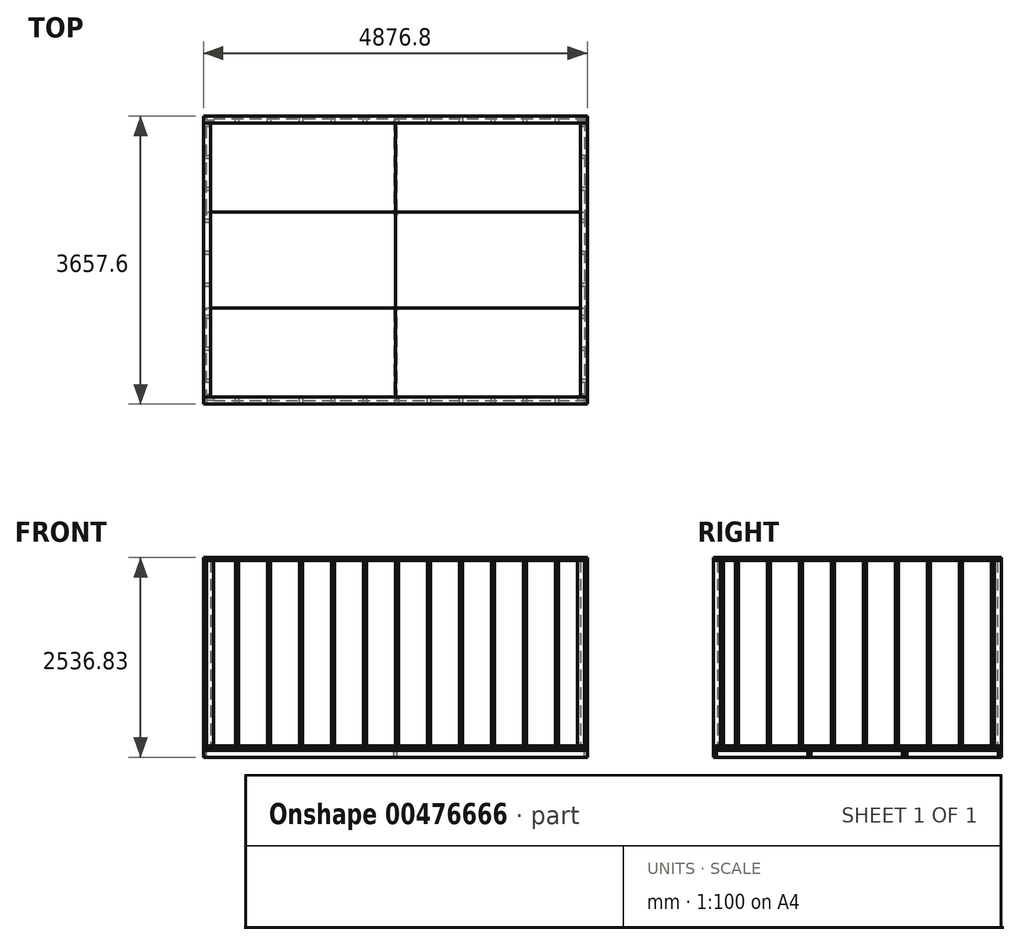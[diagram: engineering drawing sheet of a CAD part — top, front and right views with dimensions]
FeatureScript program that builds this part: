
annotation { "Feature Type Name" : "Feature", "Feature Type Description" : "" }
export const myFeature = defineFeature(function(context is Context, id is Id, definition is map)
    precondition{}
    {
        {
            var Q0;
            Q0=qCreatedBy(makeId("Top.planeOp"),FACE);
            var sketch = newSketch(context, id + "F0", { "sketchPlane" : qUnion([Q0])});
            skLineSegment(sketch, "E0.bottom", {"start": v(0, 0) * mm, "end": v(2438.4, 0) * mm});
            skLineSegment(sketch, "E0.top", {"start": v(0, 1219.2) * mm, "end": v(2438.4, 1219.2) * mm});
            skLineSegment(sketch, "E0.left", {"start": v(0, 0) * mm, "end": v(0, 1219.2) * mm});
            skLineSegment(sketch, "E0.right", {"start": v(2438.4, 0) * mm, "end": v(2438.4, 1219.2) * mm});
            skSolve(sketch);
        }
        {
            var Q0;
            Q0=makeQuery(id+"F0.imprint","IMPRINT",FACE,{"disambiguationData":[TD([[makeQuery(id+"F0.imprint","IMPRINT",EDGE,{"derivedFrom":sQuery(id+"F0.wireOp",EDGE,"E0.bottom")}),1.0]])]});
            extrude(context, id + "F1", {"entities" : qUnion([Q0]), "oppositeDirection" : true, "depth" : 19.05 * mm});
        }
        {
            var Q0;
            Q0=makeQuery(id+"F1.opExtrude","SWEPT_BODY",BODY,{"disambiguationData":[OSD([sQuery(id+"F0.wireOp",EDGE,"E0.bottom"),sQuery(id+"F0.wireOp",EDGE,"E0.top"),sQuery(id+"F0.wireOp",EDGE,"E0.left"),sQuery(id+"F0.wireOp",EDGE,"E0.right")])]});
            transform(context, id + "F2", {"entities" : qUnion([Q0]), "transformType" : TransformType.TRANSLATION_3D, "dx" : 2438.4 * mm, "dy" : 0 * mm, "dz" : 0 * mm, "makeCopy" : true});
        }
        {
            var Q0;
            Q0=makeQuery(id+"F1.opExtrude","SWEPT_BODY",BODY,{"disambiguationData":[OSD([sQuery(id+"F0.wireOp",EDGE,"E0.bottom"),sQuery(id+"F0.wireOp",EDGE,"E0.top"),sQuery(id+"F0.wireOp",EDGE,"E0.left"),sQuery(id+"F0.wireOp",EDGE,"E0.right")])]});
            transform(context, id + "F3", {"entities" : qUnion([Q0]), "transformType" : TransformType.TRANSLATION_3D, "dx" : 0 * mm, "dy" : 1219.2 * mm, "dz" : 0 * mm, "makeCopy" : true});
        }
        {
            var Q0;
            Q0=makeQuery(id+"F3.opPattern","COPY",BODY,{"derivedFrom":makeQuery(id+"F1.opExtrude","SWEPT_BODY",BODY,{"disambiguationData":[OSD([sQuery(id+"F0.wireOp",EDGE,"E0.bottom"),sQuery(id+"F0.wireOp",EDGE,"E0.top"),sQuery(id+"F0.wireOp",EDGE,"E0.left"),sQuery(id+"F0.wireOp",EDGE,"E0.right")])]}),"instanceName":"1"});
            transform(context, id + "F4", {"entities" : qUnion([Q0]), "transformType" : TransformType.TRANSLATION_3D, "dx" : 2438.4 * mm, "dy" : 0 * mm, "dz" : 0 * mm, "makeCopy" : true});
        }
        {
            var Q0;
            Q0=makeQuery(id+"F3.opPattern","COPY",BODY,{"derivedFrom":makeQuery(id+"F1.opExtrude","SWEPT_BODY",BODY,{"disambiguationData":[OSD([sQuery(id+"F0.wireOp",EDGE,"E0.bottom"),sQuery(id+"F0.wireOp",EDGE,"E0.top"),sQuery(id+"F0.wireOp",EDGE,"E0.left"),sQuery(id+"F0.wireOp",EDGE,"E0.right")])]}),"instanceName":"1"});
            transform(context, id + "F5", {"entities" : qUnion([Q0]), "transformType" : TransformType.TRANSLATION_3D, "dx" : 0 * mm, "dy" : 1219.2 * mm, "dz" : 0 * mm, "makeCopy" : true});
        }
        {
            var Q0;
            Q0=makeQuery(id+"F4.opPattern","COPY",BODY,{"derivedFrom":makeQuery(id+"F3.opPattern","COPY",BODY,{"derivedFrom":makeQuery(id+"F1.opExtrude","SWEPT_BODY",BODY,{"disambiguationData":[OSD([sQuery(id+"F0.wireOp",EDGE,"E0.bottom"),sQuery(id+"F0.wireOp",EDGE,"E0.top"),sQuery(id+"F0.wireOp",EDGE,"E0.left"),sQuery(id+"F0.wireOp",EDGE,"E0.right")])]}),"instanceName":"1"}),"instanceName":"1"});
            transform(context, id + "F6", {"entities" : qUnion([Q0]), "transformType" : TransformType.TRANSLATION_3D, "dx" : 0 * mm, "dy" : 1219.2 * mm, "dz" : 0 * mm, "makeCopy" : true});
        }
        {
            var Q0;
            Q0=qCreatedBy(makeId("Top.planeOp"),FACE);
            var sketch = newSketch(context, id + "F7", { "sketchPlane" : qUnion([Q0])});
            skLineSegment(sketch, "E1.bottom", {"start": v(0, 0) * mm, "end": v(4876.8, 0) * mm});
            skLineSegment(sketch, "E1.top", {"start": v(0, 88.9) * mm, "end": v(4876.8, 88.9) * mm});
            skLineSegment(sketch, "E1.left", {"start": v(0, 0) * mm, "end": v(0, 88.9) * mm});
            skLineSegment(sketch, "E1.right", {"start": v(4876.8, 0) * mm, "end": v(4876.8, 88.9) * mm});
            skSolve(sketch);
        }
        {
            var Q0;
            Q0 = qSketchRegion(id + "F7", true);
            extrude(context, id + "F8", {"entities" : qUnion([Q0]), "depth" : 38.1 * mm});
        }
        {
            var Q0;
            Q0=makeQuery(id+"F2.opPattern","COPY",FACE,{"derivedFrom":makeQuery(id+"F1.opExtrude","CAP_FACE",FACE,{"disambiguationData":[OSD([sQuery(id+"F0.wireOp",EDGE,"E0.bottom"),sQuery(id+"F0.wireOp",EDGE,"E0.top"),sQuery(id+"F0.wireOp",EDGE,"E0.left"),sQuery(id+"F0.wireOp",EDGE,"E0.right")])],"isStart":false}),"instanceName":"1"});
            var sketch = newSketch(context, id + "F9", { "sketchPlane" : qUnion([Q0])});
            skLineSegment(sketch, "E2.bottom", {"start": v(4876.8, 0) * mm, "end": v(0, 0) * mm});
            skLineSegment(sketch, "E2.top", {"start": v(4876.8, -38.1) * mm, "end": v(0, -38.1) * mm});
            skLineSegment(sketch, "E2.left", {"start": v(4876.8, 0) * mm, "end": v(4876.8, -38.1) * mm});
            skLineSegment(sketch, "E2.right", {"start": v(0, 0) * mm, "end": v(0, -38.1) * mm});
            skSolve(sketch);
        }
        {
            var Q0;
            Q0 = qSketchRegion(id + "F9", true);
            extrude(context, id + "F10", {"entities" : qUnion([Q0]), "depth" : 88.9 * mm});
        }
        {
            var Q0;
            Q0=makeQuery(id+"F10.opExtrude","SWEPT_BODY",BODY,{"disambiguationData":[OSD([sQuery(id+"F9.wireOp",EDGE,"E2.bottom"),sQuery(id+"F9.wireOp",EDGE,"E2.top"),sQuery(id+"F9.wireOp",EDGE,"E2.left"),sQuery(id+"F9.wireOp",EDGE,"E2.right")])]});
            transform(context, id + "F11", {"entities" : qUnion([Q0]), "transformType" : TransformType.TRANSLATION_3D, "dx" : 0 * mm, "dy" : 1200.15 * mm, "dz" : 0 * mm, "makeCopy" : true});
        }
        {
            var Q0;
            Q0=makeQuery(id+"F11.opPattern","COPY",BODY,{"derivedFrom":makeQuery(id+"F10.opExtrude","SWEPT_BODY",BODY,{"disambiguationData":[OSD([sQuery(id+"F9.wireOp",EDGE,"E2.bottom"),sQuery(id+"F9.wireOp",EDGE,"E2.top"),sQuery(id+"F9.wireOp",EDGE,"E2.left"),sQuery(id+"F9.wireOp",EDGE,"E2.right")])]}),"instanceName":"1"});
            transform(context, id + "F12", {"entities" : qUnion([Q0]), "transformType" : TransformType.TRANSLATION_3D, "dx" : 0 * mm, "dy" : 1219.2 * mm, "dz" : 0 * mm, "makeCopy" : true});
        }
        {
            var Q0;
            Q0=makeQuery(id+"F12.opPattern","COPY",BODY,{"derivedFrom":makeQuery(id+"F11.opPattern","COPY",BODY,{"derivedFrom":makeQuery(id+"F10.opExtrude","SWEPT_BODY",BODY,{"disambiguationData":[OSD([sQuery(id+"F9.wireOp",EDGE,"E2.bottom"),sQuery(id+"F9.wireOp",EDGE,"E2.top"),sQuery(id+"F9.wireOp",EDGE,"E2.left"),sQuery(id+"F9.wireOp",EDGE,"E2.right")])]}),"instanceName":"1"}),"instanceName":"1"});
            transform(context, id + "F13", {"entities" : qUnion([Q0]), "transformType" : TransformType.TRANSLATION_3D, "dx" : 0 * mm, "dy" : 1200.15 * mm, "dz" : 0 * mm, "makeCopy" : true});
        }
        {
            var Q0;
            Q0=makeQuery(id+"F6.opPattern","COPY",FACE,{"derivedFrom":makeQuery(id+"F4.opPattern","COPY",FACE,{"derivedFrom":makeQuery(id+"F3.opPattern","COPY",FACE,{"derivedFrom":makeQuery(id+"F1.opExtrude","CAP_FACE",FACE,{"disambiguationData":[OSD([sQuery(id+"F0.wireOp",EDGE,"E0.bottom"),sQuery(id+"F0.wireOp",EDGE,"E0.top"),sQuery(id+"F0.wireOp",EDGE,"E0.left"),sQuery(id+"F0.wireOp",EDGE,"E0.right")])],"isStart":false}),"instanceName":"1"}),"instanceName":"1"}),"instanceName":"1"});
            var sketch = newSketch(context, id + "F14", { "sketchPlane" : qUnion([Q0])});
            skLineSegment(sketch, "E3.bottom", {"start": v(4876.8, -3617.88) * mm, "end": v(4838.7, -3617.88) * mm});
            skLineSegment(sketch, "E3.top", {"start": v(4876.8, -2455.83) * mm, "end": v(4838.7, -2455.83) * mm});
            skLineSegment(sketch, "E3.left", {"start": v(4876.8, -3617.88) * mm, "end": v(4876.8, -2455.83) * mm});
            skLineSegment(sketch, "E3.right", {"start": v(4838.7, -3617.88) * mm, "end": v(4838.7, -2455.83) * mm});
            skSolve(sketch);
        }
        {
            var Q0;
            Q0 = qSketchRegion(id + "F14", true);
            extrude(context, id + "F15", {"entities" : qUnion([Q0]), "depth" : 88.9 * mm});
        }
        {
            var Q0;
            Q0=makeQuery(id+"F15.opExtrude","SWEPT_BODY",BODY,{"disambiguationData":[OSD([sQuery(id+"F14.wireOp",EDGE,"E3.bottom"),sQuery(id+"F14.wireOp",EDGE,"E3.top"),sQuery(id+"F14.wireOp",EDGE,"E3.left"),sQuery(id+"F14.wireOp",EDGE,"E3.right")])]});
            var Q1;
            Q1=makeQuery(id+"F15.opExtrude","CAP_VERTEX",VERTEX,{"disambiguationData":[OSD([sQuery(id+"F0.wireOp",EDGE,"E0.right"),sQuery(id+"F14.wireOp",EDGE,"E3.bottom"),sQuery(id+"F14.wireOp",EDGE,"E3.left")])],"isStart":true});
            var Q2;
            Q2=makeQuery(id+"F13.opPattern","COPY",VERTEX,{"derivedFrom":makeQuery(id+"F12.opPattern","COPY",VERTEX,{"derivedFrom":makeQuery(id+"F11.opPattern","COPY",VERTEX,{"derivedFrom":makeQuery(id+"F10.opExtrude","CAP_VERTEX",VERTEX,{"disambiguationData":[OSD([sQuery(id+"F9.wireOp",EDGE,"E2.bottom"),sQuery(id+"F9.wireOp",EDGE,"E2.left")])],"isStart":true}),"instanceName":"1"}),"instanceName":"1"}),"instanceName":"1"});
            transform(context, id + "F16", {"entities" : qUnion([Q0]), "transformType" : TransformType.TRANSLATION_ENTITY, "oppositeDirectionEntity" : false, "transformLine" : qUnion([Q1, Q2]), "makeCopy" : false});
        }
        {
            var Q0;
            Q0=makeQuery(id+"F15.opExtrude","SWEPT_BODY",BODY,{"disambiguationData":[OSD([sQuery(id+"F14.wireOp",EDGE,"E3.bottom"),sQuery(id+"F14.wireOp",EDGE,"E3.top"),sQuery(id+"F14.wireOp",EDGE,"E3.left"),sQuery(id+"F14.wireOp",EDGE,"E3.right")])]});
            transform(context, id + "F17", {"entities" : qUnion([Q0]), "transformType" : TransformType.TRANSLATION_3D, "dx" : -2438.4 * mm, "dy" : 0 * mm, "dz" : 0 * mm, "makeCopy" : true});
        }
        {
            var Q0;
            Q0=makeQuery(id+"F17.opPattern","COPY",BODY,{"derivedFrom":makeQuery(id+"F15.opExtrude","SWEPT_BODY",BODY,{"disambiguationData":[OSD([sQuery(id+"F14.wireOp",EDGE,"E3.bottom"),sQuery(id+"F14.wireOp",EDGE,"E3.top"),sQuery(id+"F14.wireOp",EDGE,"E3.left"),sQuery(id+"F14.wireOp",EDGE,"E3.right")])]}),"instanceName":"1"});
            transform(context, id + "F18", {"entities" : qUnion([Q0]), "transformType" : TransformType.TRANSLATION_3D, "dx" : 19.05 * mm, "dy" : 0 * mm, "dz" : 0 * mm, "makeCopy" : false});
        }
        {
            var Q0;
            Q0=makeQuery(id+"F17.opPattern","COPY",BODY,{"derivedFrom":makeQuery(id+"F15.opExtrude","SWEPT_BODY",BODY,{"disambiguationData":[OSD([sQuery(id+"F14.wireOp",EDGE,"E3.bottom"),sQuery(id+"F14.wireOp",EDGE,"E3.top"),sQuery(id+"F14.wireOp",EDGE,"E3.left"),sQuery(id+"F14.wireOp",EDGE,"E3.right")])]}),"instanceName":"1"});
            transform(context, id + "F19", {"entities" : qUnion([Q0]), "transformType" : TransformType.TRANSLATION_3D, "dx" : -2419.35 * mm, "dy" : 0 * mm, "dz" : 0 * mm, "makeCopy" : true});
        }
        {
            var Q0;
            Q0=makeQuery(id+"F15.opExtrude","SWEPT_BODY",BODY,{"disambiguationData":[OSD([sQuery(id+"F14.wireOp",EDGE,"E3.bottom"),sQuery(id+"F14.wireOp",EDGE,"E3.top"),sQuery(id+"F14.wireOp",EDGE,"E3.left"),sQuery(id+"F14.wireOp",EDGE,"E3.right")])]});
            transform(context, id + "F20", {"entities" : qUnion([Q0]), "transformType" : TransformType.TRANSLATION_3D, "dx" : 0 * mm, "dy" : -1257.3 * mm, "dz" : 0 * mm, "makeCopy" : true});
        }
        {
            var Q0;
            Q0=makeQuery(id+"F20.opPattern","COPY",BODY,{"derivedFrom":makeQuery(id+"F15.opExtrude","SWEPT_BODY",BODY,{"disambiguationData":[OSD([sQuery(id+"F14.wireOp",EDGE,"E3.bottom"),sQuery(id+"F14.wireOp",EDGE,"E3.top"),sQuery(id+"F14.wireOp",EDGE,"E3.left"),sQuery(id+"F14.wireOp",EDGE,"E3.right")])]}),"instanceName":"1"});
            transform(context, id + "F21", {"entities" : qUnion([Q0]), "transformType" : TransformType.TRANSLATION_3D, "dx" : 0 * mm, "dy" : 38.1 * mm, "dz" : 0 * mm, "makeCopy" : false});
        }
        {
            var Q0;
            Q0=makeQuery(id+"F20.opPattern","COPY",BODY,{"derivedFrom":makeQuery(id+"F15.opExtrude","SWEPT_BODY",BODY,{"disambiguationData":[OSD([sQuery(id+"F14.wireOp",EDGE,"E3.bottom"),sQuery(id+"F14.wireOp",EDGE,"E3.top"),sQuery(id+"F14.wireOp",EDGE,"E3.left"),sQuery(id+"F14.wireOp",EDGE,"E3.right")])]}),"instanceName":"1"});
            deleteBodies(context, id + "F22", {"entities" : qUnion([Q0])});
        }
        {
            var Q0;
            Q0=makeQuery(id+"F19.opPattern","COPY",BODY,{"derivedFrom":makeQuery(id+"F17.opPattern","COPY",BODY,{"derivedFrom":makeQuery(id+"F15.opExtrude","SWEPT_BODY",BODY,{"disambiguationData":[OSD([sQuery(id+"F14.wireOp",EDGE,"E3.bottom"),sQuery(id+"F14.wireOp",EDGE,"E3.top"),sQuery(id+"F14.wireOp",EDGE,"E3.left"),sQuery(id+"F14.wireOp",EDGE,"E3.right")])]}),"instanceName":"1"}),"instanceName":"1"});
            transform(context, id + "F23", {"entities" : qUnion([Q0]), "transformType" : TransformType.TRANSLATION_3D, "dx" : 0 * mm, "dy" : -2400.3 * mm, "dz" : 0 * mm, "makeCopy" : true});
        }
        {
            var Q0;
            Q0=makeQuery(id+"F23.opPattern","COPY",BODY,{"derivedFrom":makeQuery(id+"F19.opPattern","COPY",BODY,{"derivedFrom":makeQuery(id+"F17.opPattern","COPY",BODY,{"derivedFrom":makeQuery(id+"F15.opExtrude","SWEPT_BODY",BODY,{"disambiguationData":[OSD([sQuery(id+"F14.wireOp",EDGE,"E3.bottom"),sQuery(id+"F14.wireOp",EDGE,"E3.top"),sQuery(id+"F14.wireOp",EDGE,"E3.left"),sQuery(id+"F14.wireOp",EDGE,"E3.right")])]}),"instanceName":"1"}),"instanceName":"1"}),"instanceName":"1"});
            transform(context, id + "F24", {"entities" : qUnion([Q0]), "transformType" : TransformType.TRANSLATION_3D, "dx" : 0 * mm, "dy" : -19.05 * mm, "dz" : 0 * mm, "makeCopy" : false});
        }
        {
            var Q0;
            Q0=makeQuery(id+"F17.opPattern","COPY",BODY,{"derivedFrom":makeQuery(id+"F15.opExtrude","SWEPT_BODY",BODY,{"disambiguationData":[OSD([sQuery(id+"F14.wireOp",EDGE,"E3.bottom"),sQuery(id+"F14.wireOp",EDGE,"E3.top"),sQuery(id+"F14.wireOp",EDGE,"E3.left"),sQuery(id+"F14.wireOp",EDGE,"E3.right")])]}),"instanceName":"1"});
            transform(context, id + "F25", {"entities" : qUnion([Q0]), "transformType" : TransformType.TRANSLATION_3D, "dx" : 0 * mm, "dy" : -2419.35 * mm, "dz" : 0 * mm, "makeCopy" : true});
        }
        {
            var Q0;
            Q0=makeQuery(id+"F15.opExtrude","SWEPT_BODY",BODY,{"disambiguationData":[OSD([sQuery(id+"F14.wireOp",EDGE,"E3.bottom"),sQuery(id+"F14.wireOp",EDGE,"E3.top"),sQuery(id+"F14.wireOp",EDGE,"E3.left"),sQuery(id+"F14.wireOp",EDGE,"E3.right")])]});
            transform(context, id + "F26", {"entities" : qUnion([Q0]), "transformType" : TransformType.TRANSLATION_3D, "dx" : 0 * mm, "dy" : -2419.35 * mm, "dz" : 0 * mm, "makeCopy" : true});
        }
        {
            var Q0;
            Q0=makeQuery(id+"F4.opPattern","COPY",FACE,{"derivedFrom":makeQuery(id+"F3.opPattern","COPY",FACE,{"derivedFrom":makeQuery(id+"F1.opExtrude","CAP_FACE",FACE,{"disambiguationData":[OSD([sQuery(id+"F0.wireOp",EDGE,"E0.bottom"),sQuery(id+"F0.wireOp",EDGE,"E0.top"),sQuery(id+"F0.wireOp",EDGE,"E0.left"),sQuery(id+"F0.wireOp",EDGE,"E0.right")])],"isStart":false}),"instanceName":"1"}),"instanceName":"1"});
            var sketch = newSketch(context, id + "F27", { "sketchPlane" : qUnion([Q0])});
            skSolve(sketch);
        }
        {
            var Q0;
            Q0=makeQuery(id+"F15.opExtrude","SWEPT_BODY",BODY,{"disambiguationData":[OSD([sQuery(id+"F14.wireOp",EDGE,"E3.bottom"),sQuery(id+"F14.wireOp",EDGE,"E3.top"),sQuery(id+"F14.wireOp",EDGE,"E3.left"),sQuery(id+"F14.wireOp",EDGE,"E3.right")])]});
            transform(context, id + "F28", {"entities" : qUnion([Q0]), "transformType" : TransformType.TRANSLATION_3D, "dx" : 0 * mm, "dy" : -1219.2 * mm, "dz" : 0 * mm, "makeCopy" : true});
        }
        {
            var Q0;
            Q0=makeQuery(id+"F28.opPattern","COPY",FACE,{"derivedFrom":makeQuery(id+"F15.opExtrude","SWEPT_FACE",FACE,{"disambiguationData":[OSD([sQuery(id+"F14.wireOp",EDGE,"E3.bottom")])]}),"instanceName":"1"});
            extrude(context, id + "F29", {"entities" : qUnion([Q0]), "depth" : 19.05 * mm});
        }
        {
            var Q0;
            Q0=makeQuery(id+"F29.opExtrude","SWEPT_BODY",BODY,{"disambiguationData":[OSD([sQuery(id+"F14.wireOp",EDGE,"E3.bottom")])]});
            transform(context, id + "F30", {"entities" : qUnion([Q0]), "transformType" : TransformType.TRANSLATION_3D, "dx" : -2419.35 * mm, "dy" : 0 * mm, "dz" : 0 * mm, "makeCopy" : true});
        }
        {
            var Q0;
            Q0=makeQuery(id+"F30.opPattern","COPY",BODY,{"derivedFrom":makeQuery(id+"F29.opExtrude","SWEPT_BODY",BODY,{"disambiguationData":[OSD([sQuery(id+"F14.wireOp",EDGE,"E3.bottom")])]}),"instanceName":"1"});
            transform(context, id + "F31", {"entities" : qUnion([Q0]), "transformType" : TransformType.TRANSLATION_3D, "dx" : -2419.35 * mm, "dy" : 0 * mm, "dz" : 0 * mm, "makeCopy" : true});
        }
        {
            var Q0;
            Q0=makeQuery(id+"F8.opExtrude","SWEPT_BODY",BODY,{"disambiguationData":[OSD([sQuery(id+"F7.wireOp",EDGE,"E1.bottom"),sQuery(id+"F7.wireOp",EDGE,"E1.top"),sQuery(id+"F7.wireOp",EDGE,"E1.left"),sQuery(id+"F7.wireOp",EDGE,"E1.right")])]});
            transform(context, id + "F32", {"entities" : qUnion([Q0]), "transformType" : TransformType.TRANSLATION_3D, "dx" : 0 * mm, "dy" : 3568.7 * mm, "dz" : 0 * mm, "makeCopy" : true});
        }
        {
            var Q0;
            Q0=makeQuery(id+"F32.opPattern","COPY",FACE,{"derivedFrom":makeQuery(id+"F8.opExtrude","CAP_FACE",FACE,{"disambiguationData":[OSD([sQuery(id+"F7.wireOp",EDGE,"E1.bottom"),sQuery(id+"F7.wireOp",EDGE,"E1.top"),sQuery(id+"F7.wireOp",EDGE,"E1.left"),sQuery(id+"F7.wireOp",EDGE,"E1.right")])],"isStart":false}),"instanceName":"1"});
            var sketch = newSketch(context, id + "F33", { "sketchPlane" : qUnion([Q0])});
            skLineSegment(sketch, "E4.bottom", {"start": v(0, 3568.7) * mm, "end": v(88.9, 3568.7) * mm});
            skLineSegment(sketch, "E4.top", {"start": v(0, 88.9) * mm, "end": v(88.9, 88.9) * mm});
            skLineSegment(sketch, "E4.left", {"start": v(0, 3568.7) * mm, "end": v(0, 88.9) * mm});
            skLineSegment(sketch, "E4.right", {"start": v(88.9, 3568.7) * mm, "end": v(88.9, 88.9) * mm});
            skSolve(sketch);
        }
        {
            var Q0;
            Q0=makeQuery(id+"F33.imprint","IMPRINT",FACE,{"disambiguationData":[TD([[makeQuery(id+"F33.imprint","IMPRINT",EDGE,{"derivedFrom":sQuery(id+"F33.wireOp",EDGE,"E4.bottom")}),-1.0]])]});
            extrude(context, id + "F34", {"entities" : qUnion([Q0]), "depth" : -38.1 * mm});
        }
        {
            var Q0;
            Q0=makeQuery(id+"F34.opExtrude","SWEPT_BODY",BODY,{"disambiguationData":[OSD([sQuery(id+"F33.wireOp",EDGE,"E4.bottom"),sQuery(id+"F33.wireOp",EDGE,"E4.top"),sQuery(id+"F33.wireOp",EDGE,"E4.left"),sQuery(id+"F33.wireOp",EDGE,"E4.right")])]});
            transform(context, id + "F35", {"entities" : qUnion([Q0]), "transformType" : TransformType.TRANSLATION_3D, "dx" : 4787.9 * mm, "dy" : 0 * mm, "dz" : 0 * mm, "makeCopy" : true});
        }
        {
            var Q0;
            Q0=makeQuery(id+"F32.opPattern","COPY",FACE,{"derivedFrom":makeQuery(id+"F8.opExtrude","CAP_FACE",FACE,{"disambiguationData":[OSD([sQuery(id+"F7.wireOp",EDGE,"E1.bottom"),sQuery(id+"F7.wireOp",EDGE,"E1.top"),sQuery(id+"F7.wireOp",EDGE,"E1.left"),sQuery(id+"F7.wireOp",EDGE,"E1.right")])],"isStart":false}),"instanceName":"1"});
            var sketch = newSketch(context, id + "F36", { "sketchPlane" : qUnion([Q0])});
            skLineSegment(sketch, "E5.bottom", {"start": v(0, 3657.6) * mm, "end": v(38.1, 3657.6) * mm});
            skLineSegment(sketch, "E5.top", {"start": v(0, 3568.7) * mm, "end": v(38.1, 3568.7) * mm});
            skLineSegment(sketch, "E5.left", {"start": v(0, 3657.6) * mm, "end": v(0, 3568.7) * mm});
            skLineSegment(sketch, "E5.right", {"start": v(38.1, 3657.6) * mm, "end": v(38.1, 3568.7) * mm});
            skSolve(sketch);
        }
        {
            var Q0;
            Q0=makeQuery(id+"F36.imprint","IMPRINT",FACE,{"disambiguationData":[TD([[makeQuery(id+"F36.imprint","IMPRINT",EDGE,{"derivedFrom":sQuery(id+"F36.wireOp",EDGE,"E5.bottom")}),-1.0]])]});
            extrude(context, id + "F37", {"entities" : qUnion([Q0]), "depth" : 2352.67 * mm});
        }
        {
            var Q0;
            Q0=makeQuery(id+"F37.opExtrude","SWEPT_BODY",BODY,{"disambiguationData":[OSD([sQuery(id+"F36.wireOp",EDGE,"E5.bottom"),sQuery(id+"F36.wireOp",EDGE,"E5.top"),sQuery(id+"F36.wireOp",EDGE,"E5.left"),sQuery(id+"F36.wireOp",EDGE,"E5.right")])]});
            transform(context, id + "F38", {"entities" : qUnion([Q0]), "transformType" : TransformType.TRANSLATION_3D, "dx" : 406.4 * mm, "dy" : 0 * mm, "dz" : 0 * mm, "makeCopy" : true});
        }
        {
            var Q0;
            Q0=makeQuery(id+"F38.opPattern","COPY",BODY,{"derivedFrom":makeQuery(id+"F37.opExtrude","SWEPT_BODY",BODY,{"disambiguationData":[OSD([sQuery(id+"F36.wireOp",EDGE,"E5.bottom"),sQuery(id+"F36.wireOp",EDGE,"E5.top"),sQuery(id+"F36.wireOp",EDGE,"E5.left"),sQuery(id+"F36.wireOp",EDGE,"E5.right")])]}),"instanceName":"1"});
            transform(context, id + "F39", {"entities" : qUnion([Q0]), "transformType" : TransformType.TRANSLATION_3D, "dx" : 406.4 * mm, "dy" : 0 * mm, "dz" : 0 * mm, "makeCopy" : true});
        }
        {
            var Q0;
            Q0=makeQuery(id+"F39.opPattern","COPY",BODY,{"derivedFrom":makeQuery(id+"F38.opPattern","COPY",BODY,{"derivedFrom":makeQuery(id+"F37.opExtrude","SWEPT_BODY",BODY,{"disambiguationData":[OSD([sQuery(id+"F36.wireOp",EDGE,"E5.bottom"),sQuery(id+"F36.wireOp",EDGE,"E5.top"),sQuery(id+"F36.wireOp",EDGE,"E5.left"),sQuery(id+"F36.wireOp",EDGE,"E5.right")])]}),"instanceName":"1"}),"instanceName":"1"});
            transform(context, id + "F40", {"entities" : qUnion([Q0]), "transformType" : TransformType.TRANSLATION_3D, "dx" : 406.4 * mm, "dy" : 0 * mm, "dz" : 0 * mm, "makeCopy" : true});
        }
        {
            var Q0;
            Q0=makeQuery(id+"F40.opPattern","COPY",BODY,{"derivedFrom":makeQuery(id+"F39.opPattern","COPY",BODY,{"derivedFrom":makeQuery(id+"F38.opPattern","COPY",BODY,{"derivedFrom":makeQuery(id+"F37.opExtrude","SWEPT_BODY",BODY,{"disambiguationData":[OSD([sQuery(id+"F36.wireOp",EDGE,"E5.bottom"),sQuery(id+"F36.wireOp",EDGE,"E5.top"),sQuery(id+"F36.wireOp",EDGE,"E5.left"),sQuery(id+"F36.wireOp",EDGE,"E5.right")])]}),"instanceName":"1"}),"instanceName":"1"}),"instanceName":"1"});
            transform(context, id + "F41", {"entities" : qUnion([Q0]), "transformType" : TransformType.TRANSLATION_3D, "dx" : 406.4 * mm, "dy" : 0 * mm, "dz" : 0 * mm, "makeCopy" : true});
        }
        {
            var Q0;
            Q0=makeQuery(id+"F41.opPattern","COPY",BODY,{"derivedFrom":makeQuery(id+"F40.opPattern","COPY",BODY,{"derivedFrom":makeQuery(id+"F39.opPattern","COPY",BODY,{"derivedFrom":makeQuery(id+"F38.opPattern","COPY",BODY,{"derivedFrom":makeQuery(id+"F37.opExtrude","SWEPT_BODY",BODY,{"disambiguationData":[OSD([sQuery(id+"F36.wireOp",EDGE,"E5.bottom"),sQuery(id+"F36.wireOp",EDGE,"E5.top"),sQuery(id+"F36.wireOp",EDGE,"E5.left"),sQuery(id+"F36.wireOp",EDGE,"E5.right")])]}),"instanceName":"1"}),"instanceName":"1"}),"instanceName":"1"}),"instanceName":"1"});
            transform(context, id + "F42", {"entities" : qUnion([Q0]), "transformType" : TransformType.TRANSLATION_3D, "dx" : 406.4 * mm, "dy" : 0 * mm, "dz" : 0 * mm, "makeCopy" : true});
        }
        {
            var Q0;
            Q0=makeQuery(id+"F42.opPattern","COPY",BODY,{"derivedFrom":makeQuery(id+"F41.opPattern","COPY",BODY,{"derivedFrom":makeQuery(id+"F40.opPattern","COPY",BODY,{"derivedFrom":makeQuery(id+"F39.opPattern","COPY",BODY,{"derivedFrom":makeQuery(id+"F38.opPattern","COPY",BODY,{"derivedFrom":makeQuery(id+"F37.opExtrude","SWEPT_BODY",BODY,{"disambiguationData":[OSD([sQuery(id+"F36.wireOp",EDGE,"E5.bottom"),sQuery(id+"F36.wireOp",EDGE,"E5.top"),sQuery(id+"F36.wireOp",EDGE,"E5.left"),sQuery(id+"F36.wireOp",EDGE,"E5.right")])]}),"instanceName":"1"}),"instanceName":"1"}),"instanceName":"1"}),"instanceName":"1"}),"instanceName":"1"});
            transform(context, id + "F43", {"entities" : qUnion([Q0]), "transformType" : TransformType.TRANSLATION_3D, "dx" : 406.4 * mm, "dy" : 0 * mm, "dz" : 0 * mm, "makeCopy" : true});
        }
        {
            var Q0;
            Q0=makeQuery(id+"F43.opPattern","COPY",BODY,{"derivedFrom":makeQuery(id+"F42.opPattern","COPY",BODY,{"derivedFrom":makeQuery(id+"F41.opPattern","COPY",BODY,{"derivedFrom":makeQuery(id+"F40.opPattern","COPY",BODY,{"derivedFrom":makeQuery(id+"F39.opPattern","COPY",BODY,{"derivedFrom":makeQuery(id+"F38.opPattern","COPY",BODY,{"derivedFrom":makeQuery(id+"F37.opExtrude","SWEPT_BODY",BODY,{"disambiguationData":[OSD([sQuery(id+"F36.wireOp",EDGE,"E5.bottom"),sQuery(id+"F36.wireOp",EDGE,"E5.top"),sQuery(id+"F36.wireOp",EDGE,"E5.left"),sQuery(id+"F36.wireOp",EDGE,"E5.right")])]}),"instanceName":"1"}),"instanceName":"1"}),"instanceName":"1"}),"instanceName":"1"}),"instanceName":"1"}),"instanceName":"1"});
            transform(context, id + "F44", {"entities" : qUnion([Q0]), "transformType" : TransformType.TRANSLATION_3D, "dx" : 406.4 * mm, "dy" : 0 * mm, "dz" : 0 * mm, "makeCopy" : true});
        }
        {
            var Q0;
            Q0=makeQuery(id+"F44.opPattern","COPY",BODY,{"derivedFrom":makeQuery(id+"F43.opPattern","COPY",BODY,{"derivedFrom":makeQuery(id+"F42.opPattern","COPY",BODY,{"derivedFrom":makeQuery(id+"F41.opPattern","COPY",BODY,{"derivedFrom":makeQuery(id+"F40.opPattern","COPY",BODY,{"derivedFrom":makeQuery(id+"F39.opPattern","COPY",BODY,{"derivedFrom":makeQuery(id+"F38.opPattern","COPY",BODY,{"derivedFrom":makeQuery(id+"F37.opExtrude","SWEPT_BODY",BODY,{"disambiguationData":[OSD([sQuery(id+"F36.wireOp",EDGE,"E5.bottom"),sQuery(id+"F36.wireOp",EDGE,"E5.top"),sQuery(id+"F36.wireOp",EDGE,"E5.left"),sQuery(id+"F36.wireOp",EDGE,"E5.right")])]}),"instanceName":"1"}),"instanceName":"1"}),"instanceName":"1"}),"instanceName":"1"}),"instanceName":"1"}),"instanceName":"1"}),"instanceName":"1"});
            transform(context, id + "F45", {"entities" : qUnion([Q0]), "transformType" : TransformType.TRANSLATION_3D, "dx" : 406.4 * mm, "dy" : 0 * mm, "dz" : 0 * mm, "makeCopy" : true});
        }
        {
            var Q0;
            Q0=makeQuery(id+"F45.opPattern","COPY",BODY,{"derivedFrom":makeQuery(id+"F44.opPattern","COPY",BODY,{"derivedFrom":makeQuery(id+"F43.opPattern","COPY",BODY,{"derivedFrom":makeQuery(id+"F42.opPattern","COPY",BODY,{"derivedFrom":makeQuery(id+"F41.opPattern","COPY",BODY,{"derivedFrom":makeQuery(id+"F40.opPattern","COPY",BODY,{"derivedFrom":makeQuery(id+"F39.opPattern","COPY",BODY,{"derivedFrom":makeQuery(id+"F38.opPattern","COPY",BODY,{"derivedFrom":makeQuery(id+"F37.opExtrude","SWEPT_BODY",BODY,{"disambiguationData":[OSD([sQuery(id+"F36.wireOp",EDGE,"E5.bottom"),sQuery(id+"F36.wireOp",EDGE,"E5.top"),sQuery(id+"F36.wireOp",EDGE,"E5.left"),sQuery(id+"F36.wireOp",EDGE,"E5.right")])]}),"instanceName":"1"}),"instanceName":"1"}),"instanceName":"1"}),"instanceName":"1"}),"instanceName":"1"}),"instanceName":"1"}),"instanceName":"1"}),"instanceName":"1"});
            transform(context, id + "F46", {"entities" : qUnion([Q0]), "transformType" : TransformType.TRANSLATION_3D, "dx" : 406.4 * mm, "dy" : 0 * mm, "dz" : 0 * mm, "makeCopy" : true});
        }
        {
            var Q0;
            Q0=makeQuery(id+"F46.opPattern","COPY",BODY,{"derivedFrom":makeQuery(id+"F45.opPattern","COPY",BODY,{"derivedFrom":makeQuery(id+"F44.opPattern","COPY",BODY,{"derivedFrom":makeQuery(id+"F43.opPattern","COPY",BODY,{"derivedFrom":makeQuery(id+"F42.opPattern","COPY",BODY,{"derivedFrom":makeQuery(id+"F41.opPattern","COPY",BODY,{"derivedFrom":makeQuery(id+"F40.opPattern","COPY",BODY,{"derivedFrom":makeQuery(id+"F39.opPattern","COPY",BODY,{"derivedFrom":makeQuery(id+"F38.opPattern","COPY",BODY,{"derivedFrom":makeQuery(id+"F37.opExtrude","SWEPT_BODY",BODY,{"disambiguationData":[OSD([sQuery(id+"F36.wireOp",EDGE,"E5.bottom"),sQuery(id+"F36.wireOp",EDGE,"E5.top"),sQuery(id+"F36.wireOp",EDGE,"E5.left"),sQuery(id+"F36.wireOp",EDGE,"E5.right")])]}),"instanceName":"1"}),"instanceName":"1"}),"instanceName":"1"}),"instanceName":"1"}),"instanceName":"1"}),"instanceName":"1"}),"instanceName":"1"}),"instanceName":"1"}),"instanceName":"1"});
            transform(context, id + "F47", {"entities" : qUnion([Q0]), "transformType" : TransformType.TRANSLATION_3D, "dx" : 406.4 * mm, "dy" : 0 * mm, "dz" : 0 * mm, "makeCopy" : true});
        }
        {
            var Q0;
            Q0=makeQuery(id+"F47.opPattern","COPY",BODY,{"derivedFrom":makeQuery(id+"F46.opPattern","COPY",BODY,{"derivedFrom":makeQuery(id+"F45.opPattern","COPY",BODY,{"derivedFrom":makeQuery(id+"F44.opPattern","COPY",BODY,{"derivedFrom":makeQuery(id+"F43.opPattern","COPY",BODY,{"derivedFrom":makeQuery(id+"F42.opPattern","COPY",BODY,{"derivedFrom":makeQuery(id+"F41.opPattern","COPY",BODY,{"derivedFrom":makeQuery(id+"F40.opPattern","COPY",BODY,{"derivedFrom":makeQuery(id+"F39.opPattern","COPY",BODY,{"derivedFrom":makeQuery(id+"F38.opPattern","COPY",BODY,{"derivedFrom":makeQuery(id+"F37.opExtrude","SWEPT_BODY",BODY,{"disambiguationData":[OSD([sQuery(id+"F36.wireOp",EDGE,"E5.bottom"),sQuery(id+"F36.wireOp",EDGE,"E5.top"),sQuery(id+"F36.wireOp",EDGE,"E5.left"),sQuery(id+"F36.wireOp",EDGE,"E5.right")])]}),"instanceName":"1"}),"instanceName":"1"}),"instanceName":"1"}),"instanceName":"1"}),"instanceName":"1"}),"instanceName":"1"}),"instanceName":"1"}),"instanceName":"1"}),"instanceName":"1"}),"instanceName":"1"});
            transform(context, id + "F48", {"entities" : qUnion([Q0]), "transformType" : TransformType.TRANSLATION_3D, "dx" : 406.4 * mm, "dy" : 0 * mm, "dz" : 0 * mm, "makeCopy" : true});
        }
        {
            var Q0;
            Q0=makeQuery(id+"F48.opPattern","COPY",BODY,{"derivedFrom":makeQuery(id+"F47.opPattern","COPY",BODY,{"derivedFrom":makeQuery(id+"F46.opPattern","COPY",BODY,{"derivedFrom":makeQuery(id+"F45.opPattern","COPY",BODY,{"derivedFrom":makeQuery(id+"F44.opPattern","COPY",BODY,{"derivedFrom":makeQuery(id+"F43.opPattern","COPY",BODY,{"derivedFrom":makeQuery(id+"F42.opPattern","COPY",BODY,{"derivedFrom":makeQuery(id+"F41.opPattern","COPY",BODY,{"derivedFrom":makeQuery(id+"F40.opPattern","COPY",BODY,{"derivedFrom":makeQuery(id+"F39.opPattern","COPY",BODY,{"derivedFrom":makeQuery(id+"F38.opPattern","COPY",BODY,{"derivedFrom":makeQuery(id+"F37.opExtrude","SWEPT_BODY",BODY,{"disambiguationData":[OSD([sQuery(id+"F36.wireOp",EDGE,"E5.bottom"),sQuery(id+"F36.wireOp",EDGE,"E5.top"),sQuery(id+"F36.wireOp",EDGE,"E5.left"),sQuery(id+"F36.wireOp",EDGE,"E5.right")])]}),"instanceName":"1"}),"instanceName":"1"}),"instanceName":"1"}),"instanceName":"1"}),"instanceName":"1"}),"instanceName":"1"}),"instanceName":"1"}),"instanceName":"1"}),"instanceName":"1"}),"instanceName":"1"}),"instanceName":"1"});
            transform(context, id + "F49", {"entities" : qUnion([Q0]), "transformType" : TransformType.TRANSLATION_3D, "dx" : 368.3 * mm, "dy" : 0 * mm, "dz" : 0 * mm, "makeCopy" : true});
        }
        {
            var Q0;
            Q0=makeQuery(id+"F32.opPattern","COPY",BODY,{"derivedFrom":makeQuery(id+"F8.opExtrude","SWEPT_BODY",BODY,{"disambiguationData":[OSD([sQuery(id+"F7.wireOp",EDGE,"E1.bottom"),sQuery(id+"F7.wireOp",EDGE,"E1.top"),sQuery(id+"F7.wireOp",EDGE,"E1.left"),sQuery(id+"F7.wireOp",EDGE,"E1.right")])]}),"instanceName":"1"});
            transform(context, id + "F50", {"entities" : qUnion([Q0]), "transformType" : TransformType.TRANSLATION_3D, "dx" : 0 * mm, "dy" : 0 * mm, "dz" : 2390.78 * mm, "makeCopy" : true});
        }
        {
            var Q0;
            Q0=makeQuery(id+"F37.opExtrude","SWEPT_BODY",BODY,{"disambiguationData":[OSD([sQuery(id+"F36.wireOp",EDGE,"E5.bottom"),sQuery(id+"F36.wireOp",EDGE,"E5.top"),sQuery(id+"F36.wireOp",EDGE,"E5.left"),sQuery(id+"F36.wireOp",EDGE,"E5.right")])]});
            transform(context, id + "F51", {"entities" : qUnion([Q0]), "transformType" : TransformType.TRANSLATION_3D, "dx" : 0 * mm, "dy" : -3568.7 * mm, "dz" : 0 * mm, "makeCopy" : true});
        }
        {
            var Q0;
            Q0=makeQuery(id+"F51.opPattern","COPY",BODY,{"derivedFrom":makeQuery(id+"F37.opExtrude","SWEPT_BODY",BODY,{"disambiguationData":[OSD([sQuery(id+"F36.wireOp",EDGE,"E5.bottom"),sQuery(id+"F36.wireOp",EDGE,"E5.top"),sQuery(id+"F36.wireOp",EDGE,"E5.left"),sQuery(id+"F36.wireOp",EDGE,"E5.right")])]}),"instanceName":"1"});
            transform(context, id + "F52", {"entities" : qUnion([Q0]), "transformType" : TransformType.TRANSLATION_3D, "dx" : 406.4 * mm, "dy" : 0 * mm, "dz" : 0 * mm, "makeCopy" : true});
        }
        {
            var Q0;
            Q0=makeQuery(id+"F52.opPattern","COPY",BODY,{"derivedFrom":makeQuery(id+"F51.opPattern","COPY",BODY,{"derivedFrom":makeQuery(id+"F37.opExtrude","SWEPT_BODY",BODY,{"disambiguationData":[OSD([sQuery(id+"F36.wireOp",EDGE,"E5.bottom"),sQuery(id+"F36.wireOp",EDGE,"E5.top"),sQuery(id+"F36.wireOp",EDGE,"E5.left"),sQuery(id+"F36.wireOp",EDGE,"E5.right")])]}),"instanceName":"1"}),"instanceName":"1"});
            transform(context, id + "F53", {"entities" : qUnion([Q0]), "transformType" : TransformType.TRANSLATION_3D, "dx" : 406.4 * mm, "dy" : 0 * mm, "dz" : 0 * mm, "makeCopy" : true});
        }
        {
            var Q0;
            Q0=makeQuery(id+"F53.opPattern","COPY",BODY,{"derivedFrom":makeQuery(id+"F52.opPattern","COPY",BODY,{"derivedFrom":makeQuery(id+"F51.opPattern","COPY",BODY,{"derivedFrom":makeQuery(id+"F37.opExtrude","SWEPT_BODY",BODY,{"disambiguationData":[OSD([sQuery(id+"F36.wireOp",EDGE,"E5.bottom"),sQuery(id+"F36.wireOp",EDGE,"E5.top"),sQuery(id+"F36.wireOp",EDGE,"E5.left"),sQuery(id+"F36.wireOp",EDGE,"E5.right")])]}),"instanceName":"1"}),"instanceName":"1"}),"instanceName":"1"});
            transform(context, id + "F54", {"entities" : qUnion([Q0]), "transformType" : TransformType.TRANSLATION_3D, "dx" : 406.4 * mm, "dy" : 0 * mm, "dz" : 0 * mm, "makeCopy" : true});
        }
        {
            var Q0;
            Q0=makeQuery(id+"F54.opPattern","COPY",BODY,{"derivedFrom":makeQuery(id+"F53.opPattern","COPY",BODY,{"derivedFrom":makeQuery(id+"F52.opPattern","COPY",BODY,{"derivedFrom":makeQuery(id+"F51.opPattern","COPY",BODY,{"derivedFrom":makeQuery(id+"F37.opExtrude","SWEPT_BODY",BODY,{"disambiguationData":[OSD([sQuery(id+"F36.wireOp",EDGE,"E5.bottom"),sQuery(id+"F36.wireOp",EDGE,"E5.top"),sQuery(id+"F36.wireOp",EDGE,"E5.left"),sQuery(id+"F36.wireOp",EDGE,"E5.right")])]}),"instanceName":"1"}),"instanceName":"1"}),"instanceName":"1"}),"instanceName":"1"});
            transform(context, id + "F55", {"entities" : qUnion([Q0]), "transformType" : TransformType.TRANSLATION_3D, "dx" : 406.4 * mm, "dy" : 0 * mm, "dz" : 0 * mm, "makeCopy" : true});
        }
        {
            var Q0;
            Q0=makeQuery(id+"F55.opPattern","COPY",BODY,{"derivedFrom":makeQuery(id+"F54.opPattern","COPY",BODY,{"derivedFrom":makeQuery(id+"F53.opPattern","COPY",BODY,{"derivedFrom":makeQuery(id+"F52.opPattern","COPY",BODY,{"derivedFrom":makeQuery(id+"F51.opPattern","COPY",BODY,{"derivedFrom":makeQuery(id+"F37.opExtrude","SWEPT_BODY",BODY,{"disambiguationData":[OSD([sQuery(id+"F36.wireOp",EDGE,"E5.bottom"),sQuery(id+"F36.wireOp",EDGE,"E5.top"),sQuery(id+"F36.wireOp",EDGE,"E5.left"),sQuery(id+"F36.wireOp",EDGE,"E5.right")])]}),"instanceName":"1"}),"instanceName":"1"}),"instanceName":"1"}),"instanceName":"1"}),"instanceName":"1"});
            transform(context, id + "F56", {"entities" : qUnion([Q0]), "transformType" : TransformType.TRANSLATION_3D, "dx" : 406.4 * mm, "dy" : 0 * mm, "dz" : 0 * mm, "makeCopy" : true});
        }
        {
            var Q0;
            Q0=makeQuery(id+"F56.opPattern","COPY",BODY,{"derivedFrom":makeQuery(id+"F55.opPattern","COPY",BODY,{"derivedFrom":makeQuery(id+"F54.opPattern","COPY",BODY,{"derivedFrom":makeQuery(id+"F53.opPattern","COPY",BODY,{"derivedFrom":makeQuery(id+"F52.opPattern","COPY",BODY,{"derivedFrom":makeQuery(id+"F51.opPattern","COPY",BODY,{"derivedFrom":makeQuery(id+"F37.opExtrude","SWEPT_BODY",BODY,{"disambiguationData":[OSD([sQuery(id+"F36.wireOp",EDGE,"E5.bottom"),sQuery(id+"F36.wireOp",EDGE,"E5.top"),sQuery(id+"F36.wireOp",EDGE,"E5.left"),sQuery(id+"F36.wireOp",EDGE,"E5.right")])]}),"instanceName":"1"}),"instanceName":"1"}),"instanceName":"1"}),"instanceName":"1"}),"instanceName":"1"}),"instanceName":"1"});
            transform(context, id + "F57", {"entities" : qUnion([Q0]), "transformType" : TransformType.TRANSLATION_3D, "dx" : 406.4 * mm, "dy" : 0 * mm, "dz" : 0 * mm, "makeCopy" : true});
        }
        {
            var Q0;
            Q0=makeQuery(id+"F57.opPattern","COPY",BODY,{"derivedFrom":makeQuery(id+"F56.opPattern","COPY",BODY,{"derivedFrom":makeQuery(id+"F55.opPattern","COPY",BODY,{"derivedFrom":makeQuery(id+"F54.opPattern","COPY",BODY,{"derivedFrom":makeQuery(id+"F53.opPattern","COPY",BODY,{"derivedFrom":makeQuery(id+"F52.opPattern","COPY",BODY,{"derivedFrom":makeQuery(id+"F51.opPattern","COPY",BODY,{"derivedFrom":makeQuery(id+"F37.opExtrude","SWEPT_BODY",BODY,{"disambiguationData":[OSD([sQuery(id+"F36.wireOp",EDGE,"E5.bottom"),sQuery(id+"F36.wireOp",EDGE,"E5.top"),sQuery(id+"F36.wireOp",EDGE,"E5.left"),sQuery(id+"F36.wireOp",EDGE,"E5.right")])]}),"instanceName":"1"}),"instanceName":"1"}),"instanceName":"1"}),"instanceName":"1"}),"instanceName":"1"}),"instanceName":"1"}),"instanceName":"1"});
            transform(context, id + "F58", {"entities" : qUnion([Q0]), "transformType" : TransformType.TRANSLATION_3D, "dx" : 406.4 * mm, "dy" : 0 * mm, "dz" : 0 * mm, "makeCopy" : true});
        }
        {
            var Q0;
            Q0=makeQuery(id+"F58.opPattern","COPY",BODY,{"derivedFrom":makeQuery(id+"F57.opPattern","COPY",BODY,{"derivedFrom":makeQuery(id+"F56.opPattern","COPY",BODY,{"derivedFrom":makeQuery(id+"F55.opPattern","COPY",BODY,{"derivedFrom":makeQuery(id+"F54.opPattern","COPY",BODY,{"derivedFrom":makeQuery(id+"F53.opPattern","COPY",BODY,{"derivedFrom":makeQuery(id+"F52.opPattern","COPY",BODY,{"derivedFrom":makeQuery(id+"F51.opPattern","COPY",BODY,{"derivedFrom":makeQuery(id+"F37.opExtrude","SWEPT_BODY",BODY,{"disambiguationData":[OSD([sQuery(id+"F36.wireOp",EDGE,"E5.bottom"),sQuery(id+"F36.wireOp",EDGE,"E5.top"),sQuery(id+"F36.wireOp",EDGE,"E5.left"),sQuery(id+"F36.wireOp",EDGE,"E5.right")])]}),"instanceName":"1"}),"instanceName":"1"}),"instanceName":"1"}),"instanceName":"1"}),"instanceName":"1"}),"instanceName":"1"}),"instanceName":"1"}),"instanceName":"1"});
            transform(context, id + "F59", {"entities" : qUnion([Q0]), "transformType" : TransformType.TRANSLATION_3D, "dx" : 406.4 * mm, "dy" : 0 * mm, "dz" : 0 * mm, "makeCopy" : true});
        }
        {
            var Q0;
            Q0=makeQuery(id+"F59.opPattern","COPY",BODY,{"derivedFrom":makeQuery(id+"F58.opPattern","COPY",BODY,{"derivedFrom":makeQuery(id+"F57.opPattern","COPY",BODY,{"derivedFrom":makeQuery(id+"F56.opPattern","COPY",BODY,{"derivedFrom":makeQuery(id+"F55.opPattern","COPY",BODY,{"derivedFrom":makeQuery(id+"F54.opPattern","COPY",BODY,{"derivedFrom":makeQuery(id+"F53.opPattern","COPY",BODY,{"derivedFrom":makeQuery(id+"F52.opPattern","COPY",BODY,{"derivedFrom":makeQuery(id+"F51.opPattern","COPY",BODY,{"derivedFrom":makeQuery(id+"F37.opExtrude","SWEPT_BODY",BODY,{"disambiguationData":[OSD([sQuery(id+"F36.wireOp",EDGE,"E5.bottom"),sQuery(id+"F36.wireOp",EDGE,"E5.top"),sQuery(id+"F36.wireOp",EDGE,"E5.left"),sQuery(id+"F36.wireOp",EDGE,"E5.right")])]}),"instanceName":"1"}),"instanceName":"1"}),"instanceName":"1"}),"instanceName":"1"}),"instanceName":"1"}),"instanceName":"1"}),"instanceName":"1"}),"instanceName":"1"}),"instanceName":"1"});
            transform(context, id + "F60", {"entities" : qUnion([Q0]), "transformType" : TransformType.TRANSLATION_3D, "dx" : 406.4 * mm, "dy" : 0 * mm, "dz" : 0 * mm, "makeCopy" : true});
        }
        {
            var Q0;
            Q0=makeQuery(id+"F60.opPattern","COPY",BODY,{"derivedFrom":makeQuery(id+"F59.opPattern","COPY",BODY,{"derivedFrom":makeQuery(id+"F58.opPattern","COPY",BODY,{"derivedFrom":makeQuery(id+"F57.opPattern","COPY",BODY,{"derivedFrom":makeQuery(id+"F56.opPattern","COPY",BODY,{"derivedFrom":makeQuery(id+"F55.opPattern","COPY",BODY,{"derivedFrom":makeQuery(id+"F54.opPattern","COPY",BODY,{"derivedFrom":makeQuery(id+"F53.opPattern","COPY",BODY,{"derivedFrom":makeQuery(id+"F52.opPattern","COPY",BODY,{"derivedFrom":makeQuery(id+"F51.opPattern","COPY",BODY,{"derivedFrom":makeQuery(id+"F37.opExtrude","SWEPT_BODY",BODY,{"disambiguationData":[OSD([sQuery(id+"F36.wireOp",EDGE,"E5.bottom"),sQuery(id+"F36.wireOp",EDGE,"E5.top"),sQuery(id+"F36.wireOp",EDGE,"E5.left"),sQuery(id+"F36.wireOp",EDGE,"E5.right")])]}),"instanceName":"1"}),"instanceName":"1"}),"instanceName":"1"}),"instanceName":"1"}),"instanceName":"1"}),"instanceName":"1"}),"instanceName":"1"}),"instanceName":"1"}),"instanceName":"1"}),"instanceName":"1"});
            transform(context, id + "F61", {"entities" : qUnion([Q0]), "transformType" : TransformType.TRANSLATION_3D, "dx" : 406.4 * mm, "dy" : 0 * mm, "dz" : 0 * mm, "makeCopy" : true});
        }
        {
            var Q0;
            Q0=makeQuery(id+"F61.opPattern","COPY",BODY,{"derivedFrom":makeQuery(id+"F60.opPattern","COPY",BODY,{"derivedFrom":makeQuery(id+"F59.opPattern","COPY",BODY,{"derivedFrom":makeQuery(id+"F58.opPattern","COPY",BODY,{"derivedFrom":makeQuery(id+"F57.opPattern","COPY",BODY,{"derivedFrom":makeQuery(id+"F56.opPattern","COPY",BODY,{"derivedFrom":makeQuery(id+"F55.opPattern","COPY",BODY,{"derivedFrom":makeQuery(id+"F54.opPattern","COPY",BODY,{"derivedFrom":makeQuery(id+"F53.opPattern","COPY",BODY,{"derivedFrom":makeQuery(id+"F52.opPattern","COPY",BODY,{"derivedFrom":makeQuery(id+"F51.opPattern","COPY",BODY,{"derivedFrom":makeQuery(id+"F37.opExtrude","SWEPT_BODY",BODY,{"disambiguationData":[OSD([sQuery(id+"F36.wireOp",EDGE,"E5.bottom"),sQuery(id+"F36.wireOp",EDGE,"E5.top"),sQuery(id+"F36.wireOp",EDGE,"E5.left"),sQuery(id+"F36.wireOp",EDGE,"E5.right")])]}),"instanceName":"1"}),"instanceName":"1"}),"instanceName":"1"}),"instanceName":"1"}),"instanceName":"1"}),"instanceName":"1"}),"instanceName":"1"}),"instanceName":"1"}),"instanceName":"1"}),"instanceName":"1"}),"instanceName":"1"});
            transform(context, id + "F62", {"entities" : qUnion([Q0]), "transformType" : TransformType.TRANSLATION_3D, "dx" : 406.4 * mm, "dy" : 0 * mm, "dz" : 0 * mm, "makeCopy" : true});
        }
        {
            var Q0;
            Q0=makeQuery(id+"F49.opPattern","COPY",BODY,{"derivedFrom":makeQuery(id+"F48.opPattern","COPY",BODY,{"derivedFrom":makeQuery(id+"F47.opPattern","COPY",BODY,{"derivedFrom":makeQuery(id+"F46.opPattern","COPY",BODY,{"derivedFrom":makeQuery(id+"F45.opPattern","COPY",BODY,{"derivedFrom":makeQuery(id+"F44.opPattern","COPY",BODY,{"derivedFrom":makeQuery(id+"F43.opPattern","COPY",BODY,{"derivedFrom":makeQuery(id+"F42.opPattern","COPY",BODY,{"derivedFrom":makeQuery(id+"F41.opPattern","COPY",BODY,{"derivedFrom":makeQuery(id+"F40.opPattern","COPY",BODY,{"derivedFrom":makeQuery(id+"F39.opPattern","COPY",BODY,{"derivedFrom":makeQuery(id+"F38.opPattern","COPY",BODY,{"derivedFrom":makeQuery(id+"F37.opExtrude","SWEPT_BODY",BODY,{"disambiguationData":[OSD([sQuery(id+"F36.wireOp",EDGE,"E5.bottom"),sQuery(id+"F36.wireOp",EDGE,"E5.top"),sQuery(id+"F36.wireOp",EDGE,"E5.left"),sQuery(id+"F36.wireOp",EDGE,"E5.right")])]}),"instanceName":"1"}),"instanceName":"1"}),"instanceName":"1"}),"instanceName":"1"}),"instanceName":"1"}),"instanceName":"1"}),"instanceName":"1"}),"instanceName":"1"}),"instanceName":"1"}),"instanceName":"1"}),"instanceName":"1"}),"instanceName":"1"});
            transform(context, id + "F63", {"entities" : qUnion([Q0]), "transformType" : TransformType.TRANSLATION_3D, "dx" : 0 * mm, "dy" : -3568.7 * mm, "dz" : 0 * mm, "makeCopy" : true});
        }
        {
            var Q0;
            Q0=makeQuery(id+"F50.opPattern","COPY",BODY,{"derivedFrom":makeQuery(id+"F32.opPattern","COPY",BODY,{"derivedFrom":makeQuery(id+"F8.opExtrude","SWEPT_BODY",BODY,{"disambiguationData":[OSD([sQuery(id+"F7.wireOp",EDGE,"E1.bottom"),sQuery(id+"F7.wireOp",EDGE,"E1.top"),sQuery(id+"F7.wireOp",EDGE,"E1.left"),sQuery(id+"F7.wireOp",EDGE,"E1.right")])]}),"instanceName":"1"}),"instanceName":"1"});
            transform(context, id + "F64", {"entities" : qUnion([Q0]), "transformType" : TransformType.TRANSLATION_3D, "dx" : 0 * mm, "dy" : -3568.7 * mm, "dz" : 0 * mm, "makeCopy" : true});
        }
        {
            var Q0;
            Q0=makeQuery(id+"F34.opExtrude","CAP_FACE",FACE,{"disambiguationData":[OSD([sQuery(id+"F33.wireOp",EDGE,"E4.bottom"),sQuery(id+"F33.wireOp",EDGE,"E4.top"),sQuery(id+"F33.wireOp",EDGE,"E4.left"),sQuery(id+"F33.wireOp",EDGE,"E4.right")])],"isStart":true});
            var sketch = newSketch(context, id + "F65", { "sketchPlane" : qUnion([Q0])});
            skLineSegment(sketch, "E6.bottom", {"start": v(0, 3568.7) * mm, "end": v(88.9, 3568.7) * mm});
            skLineSegment(sketch, "E6.top", {"start": v(0, 3530.6) * mm, "end": v(88.9, 3530.6) * mm});
            skLineSegment(sketch, "E6.left", {"start": v(0, 3568.7) * mm, "end": v(0, 3530.6) * mm});
            skLineSegment(sketch, "E6.right", {"start": v(88.9, 3568.7) * mm, "end": v(88.9, 3530.6) * mm});
            skSolve(sketch);
        }
        {
            var Q0;
            Q0 = qSketchRegion(id + "F65", true);
            extrude(context, id + "F66", {"entities" : qUnion([Q0]), "depth" : 2352.67 * mm});
        }
        {
            var Q0;
            Q0=makeQuery(id+"F66.opExtrude","SWEPT_BODY",BODY,{"disambiguationData":[OSD([sQuery(id+"F65.wireOp",EDGE,"E6.bottom"),sQuery(id+"F65.wireOp",EDGE,"E6.top"),sQuery(id+"F65.wireOp",EDGE,"E6.left"),sQuery(id+"F65.wireOp",EDGE,"E6.right")])]});
            transform(context, id + "F67", {"entities" : qUnion([Q0]), "transformType" : TransformType.TRANSLATION_3D, "dx" : 0 * mm, "dy" : -406.4 * mm, "dz" : 0 * mm, "makeCopy" : true});
        }
        {
            var Q0;
            Q0=makeQuery(id+"F67.opPattern","COPY",BODY,{"derivedFrom":makeQuery(id+"F66.opExtrude","SWEPT_BODY",BODY,{"disambiguationData":[OSD([sQuery(id+"F65.wireOp",EDGE,"E6.bottom"),sQuery(id+"F65.wireOp",EDGE,"E6.top"),sQuery(id+"F65.wireOp",EDGE,"E6.left"),sQuery(id+"F65.wireOp",EDGE,"E6.right")])]}),"instanceName":"1"});
            transform(context, id + "F68", {"entities" : qUnion([Q0]), "transformType" : TransformType.TRANSLATION_3D, "dx" : 0 * mm, "dy" : -406.4 * mm, "dz" : 0 * mm, "makeCopy" : true});
        }
        {
            var Q0;
            Q0=makeQuery(id+"F68.opPattern","COPY",BODY,{"derivedFrom":makeQuery(id+"F67.opPattern","COPY",BODY,{"derivedFrom":makeQuery(id+"F66.opExtrude","SWEPT_BODY",BODY,{"disambiguationData":[OSD([sQuery(id+"F65.wireOp",EDGE,"E6.bottom"),sQuery(id+"F65.wireOp",EDGE,"E6.top"),sQuery(id+"F65.wireOp",EDGE,"E6.left"),sQuery(id+"F65.wireOp",EDGE,"E6.right")])]}),"instanceName":"1"}),"instanceName":"1"});
            transform(context, id + "F69", {"entities" : qUnion([Q0]), "transformType" : TransformType.TRANSLATION_3D, "dx" : 0 * mm, "dy" : -406.4 * mm, "dz" : 0 * mm, "makeCopy" : true});
        }
        {
            var Q0;
            Q0=makeQuery(id+"F69.opPattern","COPY",BODY,{"derivedFrom":makeQuery(id+"F68.opPattern","COPY",BODY,{"derivedFrom":makeQuery(id+"F67.opPattern","COPY",BODY,{"derivedFrom":makeQuery(id+"F66.opExtrude","SWEPT_BODY",BODY,{"disambiguationData":[OSD([sQuery(id+"F65.wireOp",EDGE,"E6.bottom"),sQuery(id+"F65.wireOp",EDGE,"E6.top"),sQuery(id+"F65.wireOp",EDGE,"E6.left"),sQuery(id+"F65.wireOp",EDGE,"E6.right")])]}),"instanceName":"1"}),"instanceName":"1"}),"instanceName":"1"});
            transform(context, id + "F70", {"entities" : qUnion([Q0]), "transformType" : TransformType.TRANSLATION_3D, "dx" : 0 * mm, "dy" : -406.4 * mm, "dz" : 0 * mm, "makeCopy" : true});
        }
        {
            var Q0;
            Q0=makeQuery(id+"F70.opPattern","COPY",BODY,{"derivedFrom":makeQuery(id+"F69.opPattern","COPY",BODY,{"derivedFrom":makeQuery(id+"F68.opPattern","COPY",BODY,{"derivedFrom":makeQuery(id+"F67.opPattern","COPY",BODY,{"derivedFrom":makeQuery(id+"F66.opExtrude","SWEPT_BODY",BODY,{"disambiguationData":[OSD([sQuery(id+"F65.wireOp",EDGE,"E6.bottom"),sQuery(id+"F65.wireOp",EDGE,"E6.top"),sQuery(id+"F65.wireOp",EDGE,"E6.left"),sQuery(id+"F65.wireOp",EDGE,"E6.right")])]}),"instanceName":"1"}),"instanceName":"1"}),"instanceName":"1"}),"instanceName":"1"});
            transform(context, id + "F71", {"entities" : qUnion([Q0]), "transformType" : TransformType.TRANSLATION_3D, "dx" : 0 * mm, "dy" : -406.4 * mm, "dz" : 0 * mm, "makeCopy" : true});
        }
        {
            var Q0;
            Q0=makeQuery(id+"F71.opPattern","COPY",BODY,{"derivedFrom":makeQuery(id+"F70.opPattern","COPY",BODY,{"derivedFrom":makeQuery(id+"F69.opPattern","COPY",BODY,{"derivedFrom":makeQuery(id+"F68.opPattern","COPY",BODY,{"derivedFrom":makeQuery(id+"F67.opPattern","COPY",BODY,{"derivedFrom":makeQuery(id+"F66.opExtrude","SWEPT_BODY",BODY,{"disambiguationData":[OSD([sQuery(id+"F65.wireOp",EDGE,"E6.bottom"),sQuery(id+"F65.wireOp",EDGE,"E6.top"),sQuery(id+"F65.wireOp",EDGE,"E6.left"),sQuery(id+"F65.wireOp",EDGE,"E6.right")])]}),"instanceName":"1"}),"instanceName":"1"}),"instanceName":"1"}),"instanceName":"1"}),"instanceName":"1"});
            transform(context, id + "F72", {"entities" : qUnion([Q0]), "transformType" : TransformType.TRANSLATION_3D, "dx" : 0 * mm, "dy" : -406.4 * mm, "dz" : 0 * mm, "makeCopy" : true});
        }
        {
            var Q0;
            Q0=makeQuery(id+"F72.opPattern","COPY",BODY,{"derivedFrom":makeQuery(id+"F71.opPattern","COPY",BODY,{"derivedFrom":makeQuery(id+"F70.opPattern","COPY",BODY,{"derivedFrom":makeQuery(id+"F69.opPattern","COPY",BODY,{"derivedFrom":makeQuery(id+"F68.opPattern","COPY",BODY,{"derivedFrom":makeQuery(id+"F67.opPattern","COPY",BODY,{"derivedFrom":makeQuery(id+"F66.opExtrude","SWEPT_BODY",BODY,{"disambiguationData":[OSD([sQuery(id+"F65.wireOp",EDGE,"E6.bottom"),sQuery(id+"F65.wireOp",EDGE,"E6.top"),sQuery(id+"F65.wireOp",EDGE,"E6.left"),sQuery(id+"F65.wireOp",EDGE,"E6.right")])]}),"instanceName":"1"}),"instanceName":"1"}),"instanceName":"1"}),"instanceName":"1"}),"instanceName":"1"}),"instanceName":"1"});
            transform(context, id + "F73", {"entities" : qUnion([Q0]), "transformType" : TransformType.TRANSLATION_3D, "dx" : 0 * mm, "dy" : -406.4 * mm, "dz" : 0 * mm, "makeCopy" : true});
        }
        {
            var Q0;
            Q0=makeQuery(id+"F73.opPattern","COPY",BODY,{"derivedFrom":makeQuery(id+"F72.opPattern","COPY",BODY,{"derivedFrom":makeQuery(id+"F71.opPattern","COPY",BODY,{"derivedFrom":makeQuery(id+"F70.opPattern","COPY",BODY,{"derivedFrom":makeQuery(id+"F69.opPattern","COPY",BODY,{"derivedFrom":makeQuery(id+"F68.opPattern","COPY",BODY,{"derivedFrom":makeQuery(id+"F67.opPattern","COPY",BODY,{"derivedFrom":makeQuery(id+"F66.opExtrude","SWEPT_BODY",BODY,{"disambiguationData":[OSD([sQuery(id+"F65.wireOp",EDGE,"E6.bottom"),sQuery(id+"F65.wireOp",EDGE,"E6.top"),sQuery(id+"F65.wireOp",EDGE,"E6.left"),sQuery(id+"F65.wireOp",EDGE,"E6.right")])]}),"instanceName":"1"}),"instanceName":"1"}),"instanceName":"1"}),"instanceName":"1"}),"instanceName":"1"}),"instanceName":"1"}),"instanceName":"1"});
            transform(context, id + "F74", {"entities" : qUnion([Q0]), "transformType" : TransformType.TRANSLATION_3D, "dx" : 0 * mm, "dy" : -406.4 * mm, "dz" : 0 * mm, "makeCopy" : true});
        }
        {
            var Q0;
            Q0=makeQuery(id+"F74.opPattern","COPY",BODY,{"derivedFrom":makeQuery(id+"F73.opPattern","COPY",BODY,{"derivedFrom":makeQuery(id+"F72.opPattern","COPY",BODY,{"derivedFrom":makeQuery(id+"F71.opPattern","COPY",BODY,{"derivedFrom":makeQuery(id+"F70.opPattern","COPY",BODY,{"derivedFrom":makeQuery(id+"F69.opPattern","COPY",BODY,{"derivedFrom":makeQuery(id+"F68.opPattern","COPY",BODY,{"derivedFrom":makeQuery(id+"F67.opPattern","COPY",BODY,{"derivedFrom":makeQuery(id+"F66.opExtrude","SWEPT_BODY",BODY,{"disambiguationData":[OSD([sQuery(id+"F65.wireOp",EDGE,"E6.bottom"),sQuery(id+"F65.wireOp",EDGE,"E6.top"),sQuery(id+"F65.wireOp",EDGE,"E6.left"),sQuery(id+"F65.wireOp",EDGE,"E6.right")])]}),"instanceName":"1"}),"instanceName":"1"}),"instanceName":"1"}),"instanceName":"1"}),"instanceName":"1"}),"instanceName":"1"}),"instanceName":"1"}),"instanceName":"1"});
            transform(context, id + "F75", {"entities" : qUnion([Q0]), "transformType" : TransformType.TRANSLATION_3D, "dx" : 0 * mm, "dy" : 0 * mm, "dz" : 0 * mm, "makeCopy" : true});
        }
        {
            var Q0;
            Q0=makeQuery(id+"F75.opPattern","COPY",BODY,{"derivedFrom":makeQuery(id+"F74.opPattern","COPY",BODY,{"derivedFrom":makeQuery(id+"F73.opPattern","COPY",BODY,{"derivedFrom":makeQuery(id+"F72.opPattern","COPY",BODY,{"derivedFrom":makeQuery(id+"F71.opPattern","COPY",BODY,{"derivedFrom":makeQuery(id+"F70.opPattern","COPY",BODY,{"derivedFrom":makeQuery(id+"F69.opPattern","COPY",BODY,{"derivedFrom":makeQuery(id+"F68.opPattern","COPY",BODY,{"derivedFrom":makeQuery(id+"F67.opPattern","COPY",BODY,{"derivedFrom":makeQuery(id+"F66.opExtrude","SWEPT_BODY",BODY,{"disambiguationData":[OSD([sQuery(id+"F65.wireOp",EDGE,"E6.bottom"),sQuery(id+"F65.wireOp",EDGE,"E6.top"),sQuery(id+"F65.wireOp",EDGE,"E6.left"),sQuery(id+"F65.wireOp",EDGE,"E6.right")])]}),"instanceName":"1"}),"instanceName":"1"}),"instanceName":"1"}),"instanceName":"1"}),"instanceName":"1"}),"instanceName":"1"}),"instanceName":"1"}),"instanceName":"1"}),"instanceName":"1"});
            transform(context, id + "F76", {"entities" : qUnion([Q0]), "transformType" : TransformType.TRANSLATION_3D, "dx" : 0 * mm, "dy" : -190.5 * mm, "dz" : 0 * mm, "makeCopy" : true});
        }
        {
            var Q0;
            Q0=makeQuery(id+"F34.opExtrude","SWEPT_BODY",BODY,{"disambiguationData":[OSD([sQuery(id+"F33.wireOp",EDGE,"E4.bottom"),sQuery(id+"F33.wireOp",EDGE,"E4.top"),sQuery(id+"F33.wireOp",EDGE,"E4.left"),sQuery(id+"F33.wireOp",EDGE,"E4.right")])]});
            transform(context, id + "F77", {"entities" : qUnion([Q0]), "transformType" : TransformType.TRANSLATION_3D, "dx" : 0 * mm, "dy" : 0 * mm, "dz" : 2390.78 * mm, "makeCopy" : true});
        }
        {
            var Q0;
            Q0=makeQuery(id+"F76.opPattern","COPY",BODY,{"derivedFrom":makeQuery(id+"F75.opPattern","COPY",BODY,{"derivedFrom":makeQuery(id+"F74.opPattern","COPY",BODY,{"derivedFrom":makeQuery(id+"F73.opPattern","COPY",BODY,{"derivedFrom":makeQuery(id+"F72.opPattern","COPY",BODY,{"derivedFrom":makeQuery(id+"F71.opPattern","COPY",BODY,{"derivedFrom":makeQuery(id+"F70.opPattern","COPY",BODY,{"derivedFrom":makeQuery(id+"F69.opPattern","COPY",BODY,{"derivedFrom":makeQuery(id+"F68.opPattern","COPY",BODY,{"derivedFrom":makeQuery(id+"F67.opPattern","COPY",BODY,{"derivedFrom":makeQuery(id+"F66.opExtrude","SWEPT_BODY",BODY,{"disambiguationData":[OSD([sQuery(id+"F65.wireOp",EDGE,"E6.bottom"),sQuery(id+"F65.wireOp",EDGE,"E6.top"),sQuery(id+"F65.wireOp",EDGE,"E6.left"),sQuery(id+"F65.wireOp",EDGE,"E6.right")])]}),"instanceName":"1"}),"instanceName":"1"}),"instanceName":"1"}),"instanceName":"1"}),"instanceName":"1"}),"instanceName":"1"}),"instanceName":"1"}),"instanceName":"1"}),"instanceName":"1"}),"instanceName":"1"});
            transform(context, id + "F78", {"entities" : qUnion([Q0]), "transformType" : TransformType.TRANSLATION_3D, "dx" : 4787.9 * mm, "dy" : 0 * mm, "dz" : 0 * mm, "makeCopy" : true});
        }
        {
            var Q0;
            Q0=makeQuery(id+"F75.opPattern","COPY",BODY,{"derivedFrom":makeQuery(id+"F74.opPattern","COPY",BODY,{"derivedFrom":makeQuery(id+"F73.opPattern","COPY",BODY,{"derivedFrom":makeQuery(id+"F72.opPattern","COPY",BODY,{"derivedFrom":makeQuery(id+"F71.opPattern","COPY",BODY,{"derivedFrom":makeQuery(id+"F70.opPattern","COPY",BODY,{"derivedFrom":makeQuery(id+"F69.opPattern","COPY",BODY,{"derivedFrom":makeQuery(id+"F68.opPattern","COPY",BODY,{"derivedFrom":makeQuery(id+"F67.opPattern","COPY",BODY,{"derivedFrom":makeQuery(id+"F66.opExtrude","SWEPT_BODY",BODY,{"disambiguationData":[OSD([sQuery(id+"F65.wireOp",EDGE,"E6.bottom"),sQuery(id+"F65.wireOp",EDGE,"E6.top"),sQuery(id+"F65.wireOp",EDGE,"E6.left"),sQuery(id+"F65.wireOp",EDGE,"E6.right")])]}),"instanceName":"1"}),"instanceName":"1"}),"instanceName":"1"}),"instanceName":"1"}),"instanceName":"1"}),"instanceName":"1"}),"instanceName":"1"}),"instanceName":"1"}),"instanceName":"1"});
            transform(context, id + "F79", {"entities" : qUnion([Q0]), "transformType" : TransformType.TRANSLATION_3D, "dx" : 4787.9 * mm, "dy" : 0 * mm, "dz" : 0 * mm, "makeCopy" : true});
        }
        {
            var Q0;
            Q0=makeQuery(id+"F73.opPattern","COPY",BODY,{"derivedFrom":makeQuery(id+"F72.opPattern","COPY",BODY,{"derivedFrom":makeQuery(id+"F71.opPattern","COPY",BODY,{"derivedFrom":makeQuery(id+"F70.opPattern","COPY",BODY,{"derivedFrom":makeQuery(id+"F69.opPattern","COPY",BODY,{"derivedFrom":makeQuery(id+"F68.opPattern","COPY",BODY,{"derivedFrom":makeQuery(id+"F67.opPattern","COPY",BODY,{"derivedFrom":makeQuery(id+"F66.opExtrude","SWEPT_BODY",BODY,{"disambiguationData":[OSD([sQuery(id+"F65.wireOp",EDGE,"E6.bottom"),sQuery(id+"F65.wireOp",EDGE,"E6.top"),sQuery(id+"F65.wireOp",EDGE,"E6.left"),sQuery(id+"F65.wireOp",EDGE,"E6.right")])]}),"instanceName":"1"}),"instanceName":"1"}),"instanceName":"1"}),"instanceName":"1"}),"instanceName":"1"}),"instanceName":"1"}),"instanceName":"1"});
            transform(context, id + "F80", {"entities" : qUnion([Q0]), "transformType" : TransformType.TRANSLATION_3D, "dx" : 4787.9 * mm, "dy" : 0 * mm, "dz" : 0 * mm, "makeCopy" : true});
        }
        {
            var Q0;
            Q0=makeQuery(id+"F72.opPattern","COPY",BODY,{"derivedFrom":makeQuery(id+"F71.opPattern","COPY",BODY,{"derivedFrom":makeQuery(id+"F70.opPattern","COPY",BODY,{"derivedFrom":makeQuery(id+"F69.opPattern","COPY",BODY,{"derivedFrom":makeQuery(id+"F68.opPattern","COPY",BODY,{"derivedFrom":makeQuery(id+"F67.opPattern","COPY",BODY,{"derivedFrom":makeQuery(id+"F66.opExtrude","SWEPT_BODY",BODY,{"disambiguationData":[OSD([sQuery(id+"F65.wireOp",EDGE,"E6.bottom"),sQuery(id+"F65.wireOp",EDGE,"E6.top"),sQuery(id+"F65.wireOp",EDGE,"E6.left"),sQuery(id+"F65.wireOp",EDGE,"E6.right")])]}),"instanceName":"1"}),"instanceName":"1"}),"instanceName":"1"}),"instanceName":"1"}),"instanceName":"1"}),"instanceName":"1"});
            transform(context, id + "F81", {"entities" : qUnion([Q0]), "transformType" : TransformType.TRANSLATION_3D, "dx" : 4787.9 * mm, "dy" : 0 * mm, "dz" : 0 * mm, "makeCopy" : true});
        }
        {
            var Q0;
            Q0=makeQuery(id+"F71.opPattern","COPY",BODY,{"derivedFrom":makeQuery(id+"F70.opPattern","COPY",BODY,{"derivedFrom":makeQuery(id+"F69.opPattern","COPY",BODY,{"derivedFrom":makeQuery(id+"F68.opPattern","COPY",BODY,{"derivedFrom":makeQuery(id+"F67.opPattern","COPY",BODY,{"derivedFrom":makeQuery(id+"F66.opExtrude","SWEPT_BODY",BODY,{"disambiguationData":[OSD([sQuery(id+"F65.wireOp",EDGE,"E6.bottom"),sQuery(id+"F65.wireOp",EDGE,"E6.top"),sQuery(id+"F65.wireOp",EDGE,"E6.left"),sQuery(id+"F65.wireOp",EDGE,"E6.right")])]}),"instanceName":"1"}),"instanceName":"1"}),"instanceName":"1"}),"instanceName":"1"}),"instanceName":"1"});
            transform(context, id + "F82", {"entities" : qUnion([Q0]), "transformType" : TransformType.TRANSLATION_3D, "dx" : 4787.9 * mm, "dy" : 0 * mm, "dz" : 0 * mm, "makeCopy" : true});
        }
        {
            var Q0;
            Q0=makeQuery(id+"F70.opPattern","COPY",BODY,{"derivedFrom":makeQuery(id+"F69.opPattern","COPY",BODY,{"derivedFrom":makeQuery(id+"F68.opPattern","COPY",BODY,{"derivedFrom":makeQuery(id+"F67.opPattern","COPY",BODY,{"derivedFrom":makeQuery(id+"F66.opExtrude","SWEPT_BODY",BODY,{"disambiguationData":[OSD([sQuery(id+"F65.wireOp",EDGE,"E6.bottom"),sQuery(id+"F65.wireOp",EDGE,"E6.top"),sQuery(id+"F65.wireOp",EDGE,"E6.left"),sQuery(id+"F65.wireOp",EDGE,"E6.right")])]}),"instanceName":"1"}),"instanceName":"1"}),"instanceName":"1"}),"instanceName":"1"});
            var Q1;
            Q1=makeQuery(id+"F69.opPattern","COPY",BODY,{"derivedFrom":makeQuery(id+"F68.opPattern","COPY",BODY,{"derivedFrom":makeQuery(id+"F67.opPattern","COPY",BODY,{"derivedFrom":makeQuery(id+"F66.opExtrude","SWEPT_BODY",BODY,{"disambiguationData":[OSD([sQuery(id+"F65.wireOp",EDGE,"E6.bottom"),sQuery(id+"F65.wireOp",EDGE,"E6.top"),sQuery(id+"F65.wireOp",EDGE,"E6.left"),sQuery(id+"F65.wireOp",EDGE,"E6.right")])]}),"instanceName":"1"}),"instanceName":"1"}),"instanceName":"1"});
            transform(context, id + "F83", {"entities" : qUnion([Q0, Q1]), "transformType" : TransformType.TRANSLATION_3D, "dx" : 4787.9 * mm, "dy" : 0 * mm, "dz" : 0 * mm, "makeCopy" : true});
        }
        {
            var Q0;
            Q0=makeQuery(id+"F68.opPattern","COPY",BODY,{"derivedFrom":makeQuery(id+"F67.opPattern","COPY",BODY,{"derivedFrom":makeQuery(id+"F66.opExtrude","SWEPT_BODY",BODY,{"disambiguationData":[OSD([sQuery(id+"F65.wireOp",EDGE,"E6.bottom"),sQuery(id+"F65.wireOp",EDGE,"E6.top"),sQuery(id+"F65.wireOp",EDGE,"E6.left"),sQuery(id+"F65.wireOp",EDGE,"E6.right")])]}),"instanceName":"1"}),"instanceName":"1"});
            transform(context, id + "F84", {"entities" : qUnion([Q0]), "transformType" : TransformType.TRANSLATION_3D, "dx" : 4787.9 * mm, "dy" : 0 * mm, "dz" : 0 * mm, "makeCopy" : true});
        }
        {
            var Q0;
            Q0=makeQuery(id+"F67.opPattern","COPY",BODY,{"derivedFrom":makeQuery(id+"F66.opExtrude","SWEPT_BODY",BODY,{"disambiguationData":[OSD([sQuery(id+"F65.wireOp",EDGE,"E6.bottom"),sQuery(id+"F65.wireOp",EDGE,"E6.top"),sQuery(id+"F65.wireOp",EDGE,"E6.left"),sQuery(id+"F65.wireOp",EDGE,"E6.right")])]}),"instanceName":"1"});
            transform(context, id + "F85", {"entities" : qUnion([Q0]), "transformType" : TransformType.TRANSLATION_3D, "dx" : 4787.9 * mm, "dy" : 0 * mm, "dz" : 0 * mm, "makeCopy" : true});
        }
        {
            var Q0;
            Q0=makeQuery(id+"F77.opPattern","COPY",BODY,{"derivedFrom":makeQuery(id+"F34.opExtrude","SWEPT_BODY",BODY,{"disambiguationData":[OSD([sQuery(id+"F33.wireOp",EDGE,"E4.bottom"),sQuery(id+"F33.wireOp",EDGE,"E4.top"),sQuery(id+"F33.wireOp",EDGE,"E4.left"),sQuery(id+"F33.wireOp",EDGE,"E4.right")])]}),"instanceName":"1"});
            transform(context, id + "F86", {"entities" : qUnion([Q0]), "transformType" : TransformType.TRANSLATION_3D, "dx" : 4787.9 * mm, "dy" : 0 * mm, "dz" : 0 * mm, "makeCopy" : true});
        }
        {
            var Q0;
            Q0=makeQuery(id+"F78.opPattern","COPY",BODY,{"derivedFrom":makeQuery(id+"F76.opPattern","COPY",BODY,{"derivedFrom":makeQuery(id+"F75.opPattern","COPY",BODY,{"derivedFrom":makeQuery(id+"F74.opPattern","COPY",BODY,{"derivedFrom":makeQuery(id+"F73.opPattern","COPY",BODY,{"derivedFrom":makeQuery(id+"F72.opPattern","COPY",BODY,{"derivedFrom":makeQuery(id+"F71.opPattern","COPY",BODY,{"derivedFrom":makeQuery(id+"F70.opPattern","COPY",BODY,{"derivedFrom":makeQuery(id+"F69.opPattern","COPY",BODY,{"derivedFrom":makeQuery(id+"F68.opPattern","COPY",BODY,{"derivedFrom":makeQuery(id+"F67.opPattern","COPY",BODY,{"derivedFrom":makeQuery(id+"F66.opExtrude","SWEPT_BODY",BODY,{"disambiguationData":[OSD([sQuery(id+"F65.wireOp",EDGE,"E6.bottom"),sQuery(id+"F65.wireOp",EDGE,"E6.top"),sQuery(id+"F65.wireOp",EDGE,"E6.left"),sQuery(id+"F65.wireOp",EDGE,"E6.right")])]}),"instanceName":"1"}),"instanceName":"1"}),"instanceName":"1"}),"instanceName":"1"}),"instanceName":"1"}),"instanceName":"1"}),"instanceName":"1"}),"instanceName":"1"}),"instanceName":"1"}),"instanceName":"1"}),"instanceName":"1"});
            transform(context, id + "F87", {"entities" : qUnion([Q0]), "transformType" : TransformType.TRANSLATION_3D, "dx" : -44.45 * mm, "dy" : -38.1 * mm, "dz" : 0 * mm, "makeCopy" : true});
        }
        {
            var Q0;
            Q0=makeQuery(id+"F87.opPattern","COPY",BODY,{"derivedFrom":makeQuery(id+"F78.opPattern","COPY",BODY,{"derivedFrom":makeQuery(id+"F76.opPattern","COPY",BODY,{"derivedFrom":makeQuery(id+"F75.opPattern","COPY",BODY,{"derivedFrom":makeQuery(id+"F74.opPattern","COPY",BODY,{"derivedFrom":makeQuery(id+"F73.opPattern","COPY",BODY,{"derivedFrom":makeQuery(id+"F72.opPattern","COPY",BODY,{"derivedFrom":makeQuery(id+"F71.opPattern","COPY",BODY,{"derivedFrom":makeQuery(id+"F70.opPattern","COPY",BODY,{"derivedFrom":makeQuery(id+"F69.opPattern","COPY",BODY,{"derivedFrom":makeQuery(id+"F68.opPattern","COPY",BODY,{"derivedFrom":makeQuery(id+"F67.opPattern","COPY",BODY,{"derivedFrom":makeQuery(id+"F66.opExtrude","SWEPT_BODY",BODY,{"disambiguationData":[OSD([sQuery(id+"F65.wireOp",EDGE,"E6.bottom"),sQuery(id+"F65.wireOp",EDGE,"E6.top"),sQuery(id+"F65.wireOp",EDGE,"E6.left"),sQuery(id+"F65.wireOp",EDGE,"E6.right")])]}),"instanceName":"1"}),"instanceName":"1"}),"instanceName":"1"}),"instanceName":"1"}),"instanceName":"1"}),"instanceName":"1"}),"instanceName":"1"}),"instanceName":"1"}),"instanceName":"1"}),"instanceName":"1"}),"instanceName":"1"}),"instanceName":"1"});
            var Q1;
            Q1=makeQuery(id+"F63.opPattern","COPY",BODY,{"derivedFrom":makeQuery(id+"F49.opPattern","COPY",BODY,{"derivedFrom":makeQuery(id+"F48.opPattern","COPY",BODY,{"derivedFrom":makeQuery(id+"F47.opPattern","COPY",BODY,{"derivedFrom":makeQuery(id+"F46.opPattern","COPY",BODY,{"derivedFrom":makeQuery(id+"F45.opPattern","COPY",BODY,{"derivedFrom":makeQuery(id+"F44.opPattern","COPY",BODY,{"derivedFrom":makeQuery(id+"F43.opPattern","COPY",BODY,{"derivedFrom":makeQuery(id+"F42.opPattern","COPY",BODY,{"derivedFrom":makeQuery(id+"F41.opPattern","COPY",BODY,{"derivedFrom":makeQuery(id+"F40.opPattern","COPY",BODY,{"derivedFrom":makeQuery(id+"F39.opPattern","COPY",BODY,{"derivedFrom":makeQuery(id+"F38.opPattern","COPY",BODY,{"derivedFrom":makeQuery(id+"F37.opExtrude","SWEPT_BODY",BODY,{"disambiguationData":[OSD([sQuery(id+"F36.wireOp",EDGE,"E5.bottom"),sQuery(id+"F36.wireOp",EDGE,"E5.top"),sQuery(id+"F36.wireOp",EDGE,"E5.left"),sQuery(id+"F36.wireOp",EDGE,"E5.right")])]}),"instanceName":"1"}),"instanceName":"1"}),"instanceName":"1"}),"instanceName":"1"}),"instanceName":"1"}),"instanceName":"1"}),"instanceName":"1"}),"instanceName":"1"}),"instanceName":"1"}),"instanceName":"1"}),"instanceName":"1"}),"instanceName":"1"}),"instanceName":"1"});
            transform(context, id + "F88", {"entities" : qUnion([Q0, Q1]), "transformType" : TransformType.TRANSLATION_3D, "dx" : 6.35 * mm, "dy" : 0 * mm, "dz" : 0 * mm, "makeCopy" : false});
        }
        {
            var Q0;
            Q0=makeQuery(id+"F87.opPattern","COPY",BODY,{"derivedFrom":makeQuery(id+"F78.opPattern","COPY",BODY,{"derivedFrom":makeQuery(id+"F76.opPattern","COPY",BODY,{"derivedFrom":makeQuery(id+"F75.opPattern","COPY",BODY,{"derivedFrom":makeQuery(id+"F74.opPattern","COPY",BODY,{"derivedFrom":makeQuery(id+"F73.opPattern","COPY",BODY,{"derivedFrom":makeQuery(id+"F72.opPattern","COPY",BODY,{"derivedFrom":makeQuery(id+"F71.opPattern","COPY",BODY,{"derivedFrom":makeQuery(id+"F70.opPattern","COPY",BODY,{"derivedFrom":makeQuery(id+"F69.opPattern","COPY",BODY,{"derivedFrom":makeQuery(id+"F68.opPattern","COPY",BODY,{"derivedFrom":makeQuery(id+"F67.opPattern","COPY",BODY,{"derivedFrom":makeQuery(id+"F66.opExtrude","SWEPT_BODY",BODY,{"disambiguationData":[OSD([sQuery(id+"F65.wireOp",EDGE,"E6.bottom"),sQuery(id+"F65.wireOp",EDGE,"E6.top"),sQuery(id+"F65.wireOp",EDGE,"E6.left"),sQuery(id+"F65.wireOp",EDGE,"E6.right")])]}),"instanceName":"1"}),"instanceName":"1"}),"instanceName":"1"}),"instanceName":"1"}),"instanceName":"1"}),"instanceName":"1"}),"instanceName":"1"}),"instanceName":"1"}),"instanceName":"1"}),"instanceName":"1"}),"instanceName":"1"}),"instanceName":"1"});
            transform(context, id + "F89", {"entities" : qUnion([Q0]), "transformType" : TransformType.TRANSLATION_3D, "dx" : 6.35 * mm, "dy" : 0 * mm, "dz" : 0 * mm, "makeCopy" : false});
        }
        {
            var Q0;
            Q0=makeQuery(id+"F76.opPattern","COPY",BODY,{"derivedFrom":makeQuery(id+"F75.opPattern","COPY",BODY,{"derivedFrom":makeQuery(id+"F74.opPattern","COPY",BODY,{"derivedFrom":makeQuery(id+"F73.opPattern","COPY",BODY,{"derivedFrom":makeQuery(id+"F72.opPattern","COPY",BODY,{"derivedFrom":makeQuery(id+"F71.opPattern","COPY",BODY,{"derivedFrom":makeQuery(id+"F70.opPattern","COPY",BODY,{"derivedFrom":makeQuery(id+"F69.opPattern","COPY",BODY,{"derivedFrom":makeQuery(id+"F68.opPattern","COPY",BODY,{"derivedFrom":makeQuery(id+"F67.opPattern","COPY",BODY,{"derivedFrom":makeQuery(id+"F66.opExtrude","SWEPT_BODY",BODY,{"disambiguationData":[OSD([sQuery(id+"F65.wireOp",EDGE,"E6.bottom"),sQuery(id+"F65.wireOp",EDGE,"E6.top"),sQuery(id+"F65.wireOp",EDGE,"E6.left"),sQuery(id+"F65.wireOp",EDGE,"E6.right")])]}),"instanceName":"1"}),"instanceName":"1"}),"instanceName":"1"}),"instanceName":"1"}),"instanceName":"1"}),"instanceName":"1"}),"instanceName":"1"}),"instanceName":"1"}),"instanceName":"1"}),"instanceName":"1"});
            transform(context, id + "F90", {"entities" : qUnion([Q0]), "transformType" : TransformType.TRANSLATION_3D, "dx" : 38.1 * mm, "dy" : -38.1 * mm, "dz" : 0 * mm, "makeCopy" : true});
        }
        {
            var Q0;
            Q0=makeQuery(id+"F66.opExtrude","SWEPT_BODY",BODY,{"disambiguationData":[OSD([sQuery(id+"F65.wireOp",EDGE,"E6.bottom"),sQuery(id+"F65.wireOp",EDGE,"E6.top"),sQuery(id+"F65.wireOp",EDGE,"E6.left"),sQuery(id+"F65.wireOp",EDGE,"E6.right")])]});
            transform(context, id + "F91", {"entities" : qUnion([Q0]), "transformType" : TransformType.TRANSLATION_3D, "dx" : 38.1 * mm, "dy" : 38.1 * mm, "dz" : 0 * mm, "makeCopy" : true});
        }
        {
            var Q0;
            Q0=makeQuery(id+"F66.opExtrude","SWEPT_BODY",BODY,{"disambiguationData":[OSD([sQuery(id+"F65.wireOp",EDGE,"E6.bottom"),sQuery(id+"F65.wireOp",EDGE,"E6.top"),sQuery(id+"F65.wireOp",EDGE,"E6.left"),sQuery(id+"F65.wireOp",EDGE,"E6.right")])]});
            transform(context, id + "F92", {"entities" : qUnion([Q0]), "transformType" : TransformType.TRANSLATION_3D, "dx" : 4787.9 * mm, "dy" : 0 * mm, "dz" : 0 * mm, "makeCopy" : true});
        }
        {
            var Q0;
            Q0=makeQuery(id+"F92.opPattern","COPY",BODY,{"derivedFrom":makeQuery(id+"F66.opExtrude","SWEPT_BODY",BODY,{"disambiguationData":[OSD([sQuery(id+"F65.wireOp",EDGE,"E6.bottom"),sQuery(id+"F65.wireOp",EDGE,"E6.top"),sQuery(id+"F65.wireOp",EDGE,"E6.left"),sQuery(id+"F65.wireOp",EDGE,"E6.right")])]}),"instanceName":"1"});
            transform(context, id + "F93", {"entities" : qUnion([Q0]), "transformType" : TransformType.TRANSLATION_3D, "dx" : -38.1 * mm, "dy" : 38.1 * mm, "dz" : 0 * mm, "makeCopy" : true});
        }
        {
            var Q0;
            Q0=makeQuery(id+"F63.opPattern","COPY",BODY,{"derivedFrom":makeQuery(id+"F49.opPattern","COPY",BODY,{"derivedFrom":makeQuery(id+"F48.opPattern","COPY",BODY,{"derivedFrom":makeQuery(id+"F47.opPattern","COPY",BODY,{"derivedFrom":makeQuery(id+"F46.opPattern","COPY",BODY,{"derivedFrom":makeQuery(id+"F45.opPattern","COPY",BODY,{"derivedFrom":makeQuery(id+"F44.opPattern","COPY",BODY,{"derivedFrom":makeQuery(id+"F43.opPattern","COPY",BODY,{"derivedFrom":makeQuery(id+"F42.opPattern","COPY",BODY,{"derivedFrom":makeQuery(id+"F41.opPattern","COPY",BODY,{"derivedFrom":makeQuery(id+"F40.opPattern","COPY",BODY,{"derivedFrom":makeQuery(id+"F39.opPattern","COPY",BODY,{"derivedFrom":makeQuery(id+"F38.opPattern","COPY",BODY,{"derivedFrom":makeQuery(id+"F37.opExtrude","SWEPT_BODY",BODY,{"disambiguationData":[OSD([sQuery(id+"F36.wireOp",EDGE,"E5.bottom"),sQuery(id+"F36.wireOp",EDGE,"E5.top"),sQuery(id+"F36.wireOp",EDGE,"E5.left"),sQuery(id+"F36.wireOp",EDGE,"E5.right")])]}),"instanceName":"1"}),"instanceName":"1"}),"instanceName":"1"}),"instanceName":"1"}),"instanceName":"1"}),"instanceName":"1"}),"instanceName":"1"}),"instanceName":"1"}),"instanceName":"1"}),"instanceName":"1"}),"instanceName":"1"}),"instanceName":"1"}),"instanceName":"1"});
            transform(context, id + "F94", {"entities" : qUnion([Q0]), "transformType" : TransformType.TRANSLATION_3D, "dx" : -6.35 * mm, "dy" : 0 * mm, "dz" : 0 * mm, "makeCopy" : false});
        }
        {
            var Q0;
            Q0=makeQuery(id+"F87.opPattern","COPY",BODY,{"derivedFrom":makeQuery(id+"F78.opPattern","COPY",BODY,{"derivedFrom":makeQuery(id+"F76.opPattern","COPY",BODY,{"derivedFrom":makeQuery(id+"F75.opPattern","COPY",BODY,{"derivedFrom":makeQuery(id+"F74.opPattern","COPY",BODY,{"derivedFrom":makeQuery(id+"F73.opPattern","COPY",BODY,{"derivedFrom":makeQuery(id+"F72.opPattern","COPY",BODY,{"derivedFrom":makeQuery(id+"F71.opPattern","COPY",BODY,{"derivedFrom":makeQuery(id+"F70.opPattern","COPY",BODY,{"derivedFrom":makeQuery(id+"F69.opPattern","COPY",BODY,{"derivedFrom":makeQuery(id+"F68.opPattern","COPY",BODY,{"derivedFrom":makeQuery(id+"F67.opPattern","COPY",BODY,{"derivedFrom":makeQuery(id+"F66.opExtrude","SWEPT_BODY",BODY,{"disambiguationData":[OSD([sQuery(id+"F65.wireOp",EDGE,"E6.bottom"),sQuery(id+"F65.wireOp",EDGE,"E6.top"),sQuery(id+"F65.wireOp",EDGE,"E6.left"),sQuery(id+"F65.wireOp",EDGE,"E6.right")])]}),"instanceName":"1"}),"instanceName":"1"}),"instanceName":"1"}),"instanceName":"1"}),"instanceName":"1"}),"instanceName":"1"}),"instanceName":"1"}),"instanceName":"1"}),"instanceName":"1"}),"instanceName":"1"}),"instanceName":"1"}),"instanceName":"1"});
            transform(context, id + "F95", {"entities" : qUnion([Q0]), "transformType" : TransformType.TRANSLATION_3D, "dx" : -6.35 * mm, "dy" : 0 * mm, "dz" : 0 * mm, "makeCopy" : false});
        }
    });
